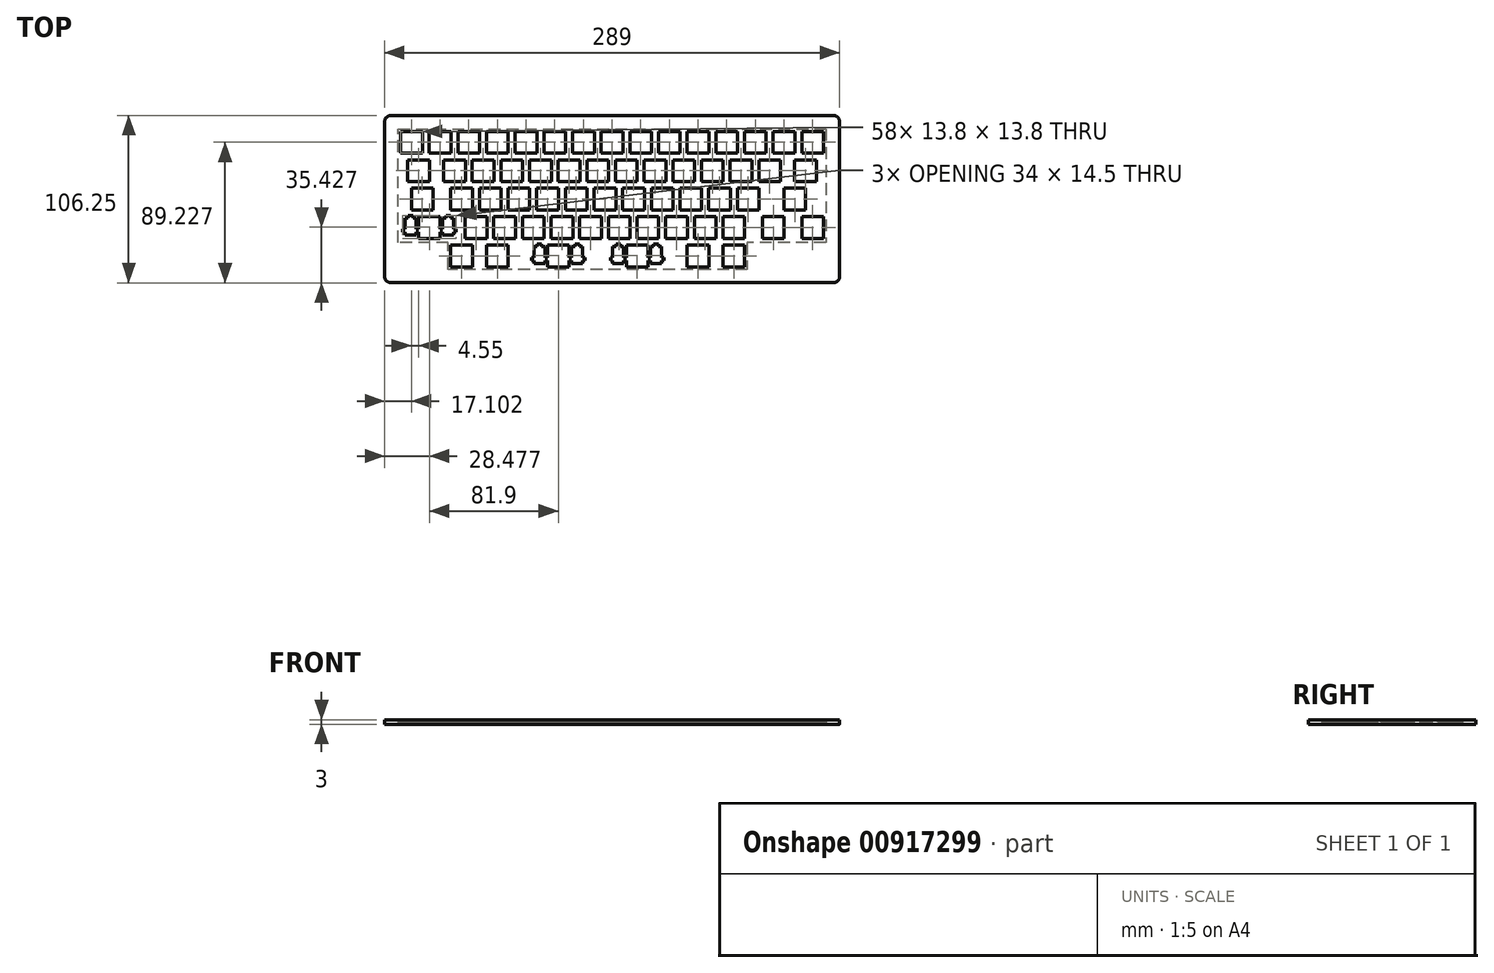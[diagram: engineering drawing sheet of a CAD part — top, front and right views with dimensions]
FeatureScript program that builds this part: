
annotation { "Feature Type Name" : "Feature", "Feature Type Description" : "" }
export const myFeature = defineFeature(function(context is Context, id is Id, definition is map)
    precondition{}
    {
        {
            var Q0;
            Q0=qCreatedBy(makeId("Top.planeOp"),FACE);
            var sketch = newSketch(context, id + "F0", { "sketchPlane" : qUnion([Q0])});
            skLineSegment(sketch, "E0.bottom", {"start": v(-54.29, -27.5) * mm, "end": v(-72.49, -27.5) * mm, "construction": true});
            skLineSegment(sketch, "E0.top", {"start": v(-54.29, -9.45) * mm, "end": v(-72.49, -9.45) * mm, "construction": true});
            skLineSegment(sketch, "E0.left", {"start": v(-54.29, -27.5) * mm, "end": v(-54.29, -9.45) * mm, "construction": true});
            skLineSegment(sketch, "E0.right", {"start": v(-72.49, -27.5) * mm, "end": v(-72.49, -9.45) * mm, "construction": true});
            skPoint(sketch, "E0.middle", {"position": v(-63.39, -18.47) * mm});
            skLineSegment(sketch, "E1.1.0.0", {"start": v(-36.09, -27.5) * mm, "end": v(-36.09, -9.45) * mm, "construction": true});
            skLineSegment(sketch, "E1.1.0.1", {"start": v(-36.09, -9.45) * mm, "end": v(-54.29, -9.45) * mm, "construction": true});
            skLineSegment(sketch, "E1.1.0.3", {"start": v(-36.09, -27.5) * mm, "end": v(-54.29, -27.5) * mm, "construction": true});
            skLineSegment(sketch, "E1.2.0.0", {"start": v(-17.89, -27.5) * mm, "end": v(-17.89, -9.45) * mm, "construction": true});
            skLineSegment(sketch, "E1.2.0.1", {"start": v(-17.89, -9.45) * mm, "end": v(-36.09, -9.45) * mm, "construction": true});
            skLineSegment(sketch, "E1.2.0.2", {"start": v(-36.09, -27.5) * mm, "end": v(-36.09, -9.45) * mm, "construction": true});
            skLineSegment(sketch, "E1.2.0.3", {"start": v(-17.89, -27.5) * mm, "end": v(-36.09, -27.5) * mm, "construction": true});
            skLineSegment(sketch, "E1.3.0.0", {"start": v(0.31, -27.5) * mm, "end": v(0.31, -9.45) * mm, "construction": true});
            skLineSegment(sketch, "E1.3.0.1", {"start": v(0.31, -9.45) * mm, "end": v(-17.89, -9.45) * mm, "construction": true});
            skLineSegment(sketch, "E1.3.0.2", {"start": v(-17.89, -27.5) * mm, "end": v(-17.89, -9.45) * mm, "construction": true});
            skLineSegment(sketch, "E1.3.0.3", {"start": v(0.31, -27.5) * mm, "end": v(-17.89, -27.5) * mm, "construction": true});
            skLineSegment(sketch, "E1.4.0.0", {"start": v(18.51, -27.5) * mm, "end": v(18.51, -9.45) * mm, "construction": true});
            skLineSegment(sketch, "E1.4.0.1", {"start": v(18.51, -9.45) * mm, "end": v(0.31, -9.45) * mm, "construction": true});
            skLineSegment(sketch, "E1.4.0.2", {"start": v(0.31, -27.5) * mm, "end": v(0.31, -9.45) * mm, "construction": true});
            skLineSegment(sketch, "E1.4.0.3", {"start": v(18.51, -27.5) * mm, "end": v(0.31, -27.5) * mm, "construction": true});
            skLineSegment(sketch, "E1.5.0.0", {"start": v(36.71, -27.5) * mm, "end": v(36.71, -9.45) * mm, "construction": true});
            skLineSegment(sketch, "E1.5.0.1", {"start": v(36.71, -9.45) * mm, "end": v(18.51, -9.45) * mm, "construction": true});
            skLineSegment(sketch, "E1.5.0.2", {"start": v(18.51, -27.5) * mm, "end": v(18.51, -9.45) * mm, "construction": true});
            skLineSegment(sketch, "E1.5.0.3", {"start": v(36.71, -27.5) * mm, "end": v(18.51, -27.5) * mm, "construction": true});
            skLineSegment(sketch, "E1.6.0.0", {"start": v(54.91, -27.5) * mm, "end": v(54.91, -9.45) * mm, "construction": true});
            skLineSegment(sketch, "E1.6.0.1", {"start": v(54.91, -9.45) * mm, "end": v(36.71, -9.45) * mm, "construction": true});
            skLineSegment(sketch, "E1.6.0.2", {"start": v(36.71, -27.5) * mm, "end": v(36.71, -9.45) * mm, "construction": true});
            skLineSegment(sketch, "E1.6.0.3", {"start": v(54.91, -27.5) * mm, "end": v(36.71, -27.5) * mm, "construction": true});
            skLineSegment(sketch, "E1.7.0.0", {"start": v(73.11, -27.5) * mm, "end": v(73.11, -9.45) * mm, "construction": true});
            skLineSegment(sketch, "E1.7.0.1", {"start": v(73.11, -9.45) * mm, "end": v(54.91, -9.45) * mm, "construction": true});
            skLineSegment(sketch, "E1.7.0.2", {"start": v(54.91, -27.5) * mm, "end": v(54.91, -9.45) * mm, "construction": true});
            skLineSegment(sketch, "E1.7.0.3", {"start": v(73.11, -27.5) * mm, "end": v(54.91, -27.5) * mm, "construction": true});
            skLineSegment(sketch, "E1.8.0.0", {"start": v(91.31, -27.5) * mm, "end": v(91.31, -9.45) * mm, "construction": true});
            skLineSegment(sketch, "E1.8.0.1", {"start": v(91.31, -9.45) * mm, "end": v(73.11, -9.45) * mm, "construction": true});
            skLineSegment(sketch, "E1.8.0.2", {"start": v(73.11, -27.5) * mm, "end": v(73.11, -9.45) * mm, "construction": true});
            skLineSegment(sketch, "E1.8.0.3", {"start": v(91.31, -27.5) * mm, "end": v(73.11, -27.5) * mm, "construction": true});
            skLineSegment(sketch, "E1.9.0.0", {"start": v(109.51, -27.5) * mm, "end": v(109.51, -9.45) * mm, "construction": true});
            skLineSegment(sketch, "E1.9.0.1", {"start": v(109.51, -9.45) * mm, "end": v(91.31, -9.45) * mm, "construction": true});
            skLineSegment(sketch, "E1.9.0.2", {"start": v(91.31, -27.5) * mm, "end": v(91.31, -9.45) * mm, "construction": true});
            skLineSegment(sketch, "E1.9.0.3", {"start": v(109.51, -27.5) * mm, "end": v(91.31, -27.5) * mm, "construction": true});
            skLineSegment(sketch, "E1.10.0.0", {"start": v(127.71, -27.5) * mm, "end": v(127.71, -9.45) * mm, "construction": true});
            skLineSegment(sketch, "E1.10.0.1", {"start": v(127.71, -9.45) * mm, "end": v(109.51, -9.45) * mm, "construction": true});
            skLineSegment(sketch, "E1.10.0.2", {"start": v(109.51, -27.5) * mm, "end": v(109.51, -9.45) * mm, "construction": true});
            skLineSegment(sketch, "E1.10.0.3", {"start": v(127.71, -27.5) * mm, "end": v(109.51, -27.5) * mm, "construction": true});
            skLineSegment(sketch, "E1.11.0.0", {"start": v(145.91, -27.5) * mm, "end": v(145.91, -9.45) * mm, "construction": true});
            skLineSegment(sketch, "E1.11.0.1", {"start": v(145.91, -9.45) * mm, "end": v(127.71, -9.45) * mm, "construction": true});
            skLineSegment(sketch, "E1.11.0.2", {"start": v(127.71, -27.5) * mm, "end": v(127.71, -9.45) * mm, "construction": true});
            skLineSegment(sketch, "E1.11.0.3", {"start": v(145.91, -27.5) * mm, "end": v(127.71, -27.5) * mm, "construction": true});
            skLineSegment(sketch, "E1.12.0.0", {"start": v(164.11, -27.5) * mm, "end": v(164.11, -9.45) * mm, "construction": true});
            skLineSegment(sketch, "E1.12.0.1", {"start": v(164.11, -9.45) * mm, "end": v(145.91, -9.45) * mm, "construction": true});
            skLineSegment(sketch, "E1.12.0.2", {"start": v(145.91, -27.5) * mm, "end": v(145.91, -9.45) * mm, "construction": true});
            skLineSegment(sketch, "E1.12.0.3", {"start": v(164.11, -27.5) * mm, "end": v(145.91, -27.5) * mm, "construction": true});
            skLineSegment(sketch, "E1.13.0.0", {"start": v(182.31, -27.5) * mm, "end": v(182.31, -9.45) * mm, "construction": true});
            skLineSegment(sketch, "E1.13.0.1", {"start": v(182.31, -9.45) * mm, "end": v(164.11, -9.45) * mm, "construction": true});
            skLineSegment(sketch, "E1.13.0.2", {"start": v(164.11, -27.5) * mm, "end": v(164.11, -9.45) * mm, "construction": true});
            skLineSegment(sketch, "E1.13.0.3", {"start": v(182.31, -27.5) * mm, "end": v(164.11, -27.5) * mm, "construction": true});
            skLineSegment(sketch, "E1.14.0.0", {"start": v(200.51, -27.5) * mm, "end": v(200.51, -9.45) * mm, "construction": true});
            skLineSegment(sketch, "E1.14.0.1", {"start": v(200.51, -9.45) * mm, "end": v(182.31, -9.45) * mm, "construction": true});
            skLineSegment(sketch, "E1.14.0.2", {"start": v(182.31, -27.5) * mm, "end": v(182.31, -9.45) * mm, "construction": true});
            skLineSegment(sketch, "E1.14.0.3", {"start": v(200.51, -27.5) * mm, "end": v(182.31, -27.5) * mm, "construction": true});
            skLineSegment(sketch, "E1.direction1", {"start": v(-72.49, -27.5) * mm, "end": v(-54.29, -27.5) * mm, "construction": true});
            skLineSegment(sketch, "E2.bottom", {"start": v(-72.49, -27.5) * mm, "end": v(-45.19, -27.5) * mm, "construction": true});
            skLineSegment(sketch, "E2.top", {"start": v(-72.49, -45.55) * mm, "end": v(-45.19, -45.55) * mm, "construction": true});
            skLineSegment(sketch, "E2.left", {"start": v(-72.49, -27.5) * mm, "end": v(-72.49, -45.55) * mm, "construction": true});
            skLineSegment(sketch, "E2.right", {"start": v(-45.19, -27.5) * mm, "end": v(-45.19, -45.55) * mm, "construction": true});
            skLineSegment(sketch, "E3.bottom", {"start": v(-45.19, -45.55) * mm, "end": v(-26.99, -45.55) * mm, "construction": true});
            skLineSegment(sketch, "E3.top", {"start": v(-45.19, -27.5) * mm, "end": v(-26.99, -27.5) * mm, "construction": true});
            skLineSegment(sketch, "E3.left", {"start": v(-45.19, -45.55) * mm, "end": v(-45.19, -27.5) * mm, "construction": true});
            skLineSegment(sketch, "E3.right", {"start": v(-26.99, -45.55) * mm, "end": v(-26.99, -27.5) * mm, "construction": true});
            skLineSegment(sketch, "E4.1.0.0", {"start": v(-26.99, -45.55) * mm, "end": v(-8.79, -45.55) * mm, "construction": true});
            skLineSegment(sketch, "E4.1.0.1", {"start": v(-26.99, -27.5) * mm, "end": v(-8.79, -27.5) * mm, "construction": true});
            skLineSegment(sketch, "E4.1.0.2", {"start": v(-26.99, -27.5) * mm, "end": v(-26.99, -45.55) * mm, "construction": true});
            skLineSegment(sketch, "E4.1.0.3", {"start": v(-8.79, -45.55) * mm, "end": v(-8.79, -27.5) * mm, "construction": true});
            skLineSegment(sketch, "E4.2.0.0", {"start": v(-8.79, -45.55) * mm, "end": v(9.41, -45.55) * mm, "construction": true});
            skLineSegment(sketch, "E4.2.0.1", {"start": v(-8.79, -27.5) * mm, "end": v(9.41, -27.5) * mm, "construction": true});
            skLineSegment(sketch, "E4.2.0.2", {"start": v(-8.79, -27.5) * mm, "end": v(-8.79, -45.55) * mm, "construction": true});
            skLineSegment(sketch, "E4.2.0.3", {"start": v(9.41, -45.55) * mm, "end": v(9.41, -27.5) * mm, "construction": true});
            skLineSegment(sketch, "E4.2.0.4", {"start": v(-8.79, -45.55) * mm, "end": v(-8.79, -27.5) * mm, "construction": true});
            skLineSegment(sketch, "E4.3.0.0", {"start": v(9.41, -45.55) * mm, "end": v(27.61, -45.55) * mm, "construction": true});
            skLineSegment(sketch, "E4.3.0.1", {"start": v(9.41, -27.5) * mm, "end": v(27.61, -27.5) * mm, "construction": true});
            skLineSegment(sketch, "E4.3.0.2", {"start": v(9.41, -27.5) * mm, "end": v(9.41, -45.55) * mm, "construction": true});
            skLineSegment(sketch, "E4.3.0.3", {"start": v(27.61, -45.55) * mm, "end": v(27.61, -27.5) * mm, "construction": true});
            skLineSegment(sketch, "E4.3.0.4", {"start": v(9.41, -45.55) * mm, "end": v(9.41, -27.5) * mm, "construction": true});
            skLineSegment(sketch, "E4.4.0.0", {"start": v(27.61, -45.55) * mm, "end": v(45.81, -45.55) * mm, "construction": true});
            skLineSegment(sketch, "E4.4.0.1", {"start": v(27.61, -27.5) * mm, "end": v(45.81, -27.5) * mm, "construction": true});
            skLineSegment(sketch, "E4.4.0.2", {"start": v(27.61, -27.5) * mm, "end": v(27.61, -45.55) * mm, "construction": true});
            skLineSegment(sketch, "E4.4.0.3", {"start": v(45.81, -45.55) * mm, "end": v(45.81, -27.5) * mm, "construction": true});
            skLineSegment(sketch, "E4.4.0.4", {"start": v(27.61, -45.55) * mm, "end": v(27.61, -27.5) * mm, "construction": true});
            skLineSegment(sketch, "E4.5.0.0", {"start": v(45.81, -45.55) * mm, "end": v(64.01, -45.55) * mm, "construction": true});
            skLineSegment(sketch, "E4.5.0.1", {"start": v(45.81, -27.5) * mm, "end": v(64.01, -27.5) * mm, "construction": true});
            skLineSegment(sketch, "E4.5.0.2", {"start": v(45.81, -27.5) * mm, "end": v(45.81, -45.55) * mm, "construction": true});
            skLineSegment(sketch, "E4.5.0.3", {"start": v(64.01, -45.55) * mm, "end": v(64.01, -27.5) * mm, "construction": true});
            skLineSegment(sketch, "E4.5.0.4", {"start": v(45.81, -45.55) * mm, "end": v(45.81, -27.5) * mm, "construction": true});
            skLineSegment(sketch, "E4.6.0.0", {"start": v(64.01, -45.55) * mm, "end": v(82.21, -45.55) * mm, "construction": true});
            skLineSegment(sketch, "E4.6.0.1", {"start": v(64.01, -27.5) * mm, "end": v(82.21, -27.5) * mm, "construction": true});
            skLineSegment(sketch, "E4.6.0.2", {"start": v(64.01, -27.5) * mm, "end": v(64.01, -45.55) * mm, "construction": true});
            skLineSegment(sketch, "E4.6.0.3", {"start": v(82.21, -45.55) * mm, "end": v(82.21, -27.5) * mm, "construction": true});
            skLineSegment(sketch, "E4.6.0.4", {"start": v(64.01, -45.55) * mm, "end": v(64.01, -27.5) * mm, "construction": true});
            skLineSegment(sketch, "E4.7.0.0", {"start": v(82.21, -45.55) * mm, "end": v(100.41, -45.55) * mm, "construction": true});
            skLineSegment(sketch, "E4.7.0.1", {"start": v(82.21, -27.5) * mm, "end": v(100.41, -27.5) * mm, "construction": true});
            skLineSegment(sketch, "E4.7.0.2", {"start": v(82.21, -27.5) * mm, "end": v(82.21, -45.55) * mm, "construction": true});
            skLineSegment(sketch, "E4.7.0.3", {"start": v(100.41, -45.55) * mm, "end": v(100.41, -27.5) * mm, "construction": true});
            skLineSegment(sketch, "E4.7.0.4", {"start": v(82.21, -45.55) * mm, "end": v(82.21, -27.5) * mm, "construction": true});
            skLineSegment(sketch, "E4.8.0.0", {"start": v(100.41, -45.55) * mm, "end": v(118.61, -45.55) * mm, "construction": true});
            skLineSegment(sketch, "E4.8.0.1", {"start": v(100.41, -27.5) * mm, "end": v(118.61, -27.5) * mm, "construction": true});
            skLineSegment(sketch, "E4.8.0.2", {"start": v(100.41, -27.5) * mm, "end": v(100.41, -45.55) * mm, "construction": true});
            skLineSegment(sketch, "E4.8.0.3", {"start": v(118.61, -45.55) * mm, "end": v(118.61, -27.5) * mm, "construction": true});
            skLineSegment(sketch, "E4.8.0.4", {"start": v(100.41, -45.55) * mm, "end": v(100.41, -27.5) * mm, "construction": true});
            skLineSegment(sketch, "E4.9.0.0", {"start": v(118.61, -45.55) * mm, "end": v(136.81, -45.55) * mm, "construction": true});
            skLineSegment(sketch, "E4.9.0.1", {"start": v(118.61, -27.5) * mm, "end": v(136.81, -27.5) * mm, "construction": true});
            skLineSegment(sketch, "E4.9.0.2", {"start": v(118.61, -27.5) * mm, "end": v(118.61, -45.55) * mm, "construction": true});
            skLineSegment(sketch, "E4.9.0.3", {"start": v(136.81, -45.55) * mm, "end": v(136.81, -27.5) * mm, "construction": true});
            skLineSegment(sketch, "E4.9.0.4", {"start": v(118.61, -45.55) * mm, "end": v(118.61, -27.5) * mm, "construction": true});
            skLineSegment(sketch, "E4.10.0.0", {"start": v(136.81, -45.55) * mm, "end": v(155.01, -45.55) * mm, "construction": true});
            skLineSegment(sketch, "E4.10.0.1", {"start": v(136.81, -27.5) * mm, "end": v(155.01, -27.5) * mm, "construction": true});
            skLineSegment(sketch, "E4.10.0.2", {"start": v(136.81, -27.5) * mm, "end": v(136.81, -45.55) * mm, "construction": true});
            skLineSegment(sketch, "E4.10.0.3", {"start": v(155.01, -45.55) * mm, "end": v(155.01, -27.5) * mm, "construction": true});
            skLineSegment(sketch, "E4.10.0.4", {"start": v(136.81, -45.55) * mm, "end": v(136.81, -27.5) * mm, "construction": true});
            skLineSegment(sketch, "E4.11.0.0", {"start": v(155.01, -45.55) * mm, "end": v(173.21, -45.55) * mm, "construction": true});
            skLineSegment(sketch, "E4.11.0.1", {"start": v(155.01, -27.5) * mm, "end": v(173.21, -27.5) * mm, "construction": true});
            skLineSegment(sketch, "E4.11.0.2", {"start": v(155.01, -27.5) * mm, "end": v(155.01, -45.55) * mm, "construction": true});
            skLineSegment(sketch, "E4.11.0.3", {"start": v(173.21, -45.55) * mm, "end": v(173.21, -27.5) * mm, "construction": true});
            skLineSegment(sketch, "E4.11.0.4", {"start": v(155.01, -45.55) * mm, "end": v(155.01, -27.5) * mm, "construction": true});
            skLineSegment(sketch, "E5.bottom", {"start": v(173.21, -45.55) * mm, "end": v(200.51, -45.55) * mm, "construction": true});
            skLineSegment(sketch, "E5.top", {"start": v(173.21, -27.5) * mm, "end": v(200.51, -27.5) * mm, "construction": true});
            skLineSegment(sketch, "E5.right", {"start": v(200.51, -45.55) * mm, "end": v(200.51, -27.5) * mm, "construction": true});
            skLineSegment(sketch, "E6.bottom", {"start": v(-72.49, -45.55) * mm, "end": v(-40.64, -45.55) * mm, "construction": true});
            skLineSegment(sketch, "E6.top", {"start": v(-72.49, -63.6) * mm, "end": v(-40.64, -63.6) * mm, "construction": true});
            skLineSegment(sketch, "E6.left", {"start": v(-72.49, -45.55) * mm, "end": v(-72.49, -63.6) * mm, "construction": true});
            skLineSegment(sketch, "E6.right", {"start": v(-40.64, -45.55) * mm, "end": v(-40.64, -63.6) * mm, "construction": true});
            skLineSegment(sketch, "E7.bottom", {"start": v(-40.64, -63.6) * mm, "end": v(-22.44, -63.6) * mm, "construction": true});
            skLineSegment(sketch, "E7.top", {"start": v(-40.64, -45.55) * mm, "end": v(-22.44, -45.55) * mm, "construction": true});
            skLineSegment(sketch, "E7.left", {"start": v(-40.64, -63.6) * mm, "end": v(-40.64, -45.55) * mm, "construction": true});
            skLineSegment(sketch, "E7.right", {"start": v(-22.44, -63.6) * mm, "end": v(-22.44, -45.55) * mm, "construction": true});
            skLineSegment(sketch, "E8.1.0.0", {"start": v(-22.44, -63.6) * mm, "end": v(-4.24, -63.6) * mm, "construction": true});
            skLineSegment(sketch, "E8.1.0.1", {"start": v(-22.44, -45.55) * mm, "end": v(-4.24, -45.55) * mm, "construction": true});
            skLineSegment(sketch, "E8.1.0.2", {"start": v(-4.24, -63.6) * mm, "end": v(-4.24, -45.55) * mm, "construction": true});
            skLineSegment(sketch, "E8.1.0.3", {"start": v(-22.44, -45.55) * mm, "end": v(-22.44, -63.6) * mm, "construction": true});
            skLineSegment(sketch, "E8.2.0.0", {"start": v(-4.24, -63.6) * mm, "end": v(13.96, -63.6) * mm, "construction": true});
            skLineSegment(sketch, "E8.2.0.1", {"start": v(-4.24, -45.55) * mm, "end": v(13.96, -45.55) * mm, "construction": true});
            skLineSegment(sketch, "E8.2.0.2", {"start": v(13.96, -63.6) * mm, "end": v(13.96, -45.55) * mm, "construction": true});
            skLineSegment(sketch, "E8.2.0.3", {"start": v(-4.24, -45.55) * mm, "end": v(-4.24, -63.6) * mm, "construction": true});
            skLineSegment(sketch, "E8.2.0.4", {"start": v(-4.24, -63.6) * mm, "end": v(-4.24, -45.55) * mm, "construction": true});
            skLineSegment(sketch, "E8.3.0.0", {"start": v(13.96, -63.6) * mm, "end": v(32.16, -63.6) * mm, "construction": true});
            skLineSegment(sketch, "E8.3.0.1", {"start": v(13.96, -45.55) * mm, "end": v(32.16, -45.55) * mm, "construction": true});
            skLineSegment(sketch, "E8.3.0.2", {"start": v(32.16, -63.6) * mm, "end": v(32.16, -45.55) * mm, "construction": true});
            skLineSegment(sketch, "E8.3.0.3", {"start": v(13.96, -45.55) * mm, "end": v(13.96, -63.6) * mm, "construction": true});
            skLineSegment(sketch, "E8.3.0.4", {"start": v(13.96, -63.6) * mm, "end": v(13.96, -45.55) * mm, "construction": true});
            skLineSegment(sketch, "E8.4.0.0", {"start": v(32.16, -63.6) * mm, "end": v(50.36, -63.6) * mm, "construction": true});
            skLineSegment(sketch, "E8.4.0.1", {"start": v(32.16, -45.55) * mm, "end": v(50.36, -45.55) * mm, "construction": true});
            skLineSegment(sketch, "E8.4.0.2", {"start": v(50.36, -63.6) * mm, "end": v(50.36, -45.55) * mm, "construction": true});
            skLineSegment(sketch, "E8.4.0.3", {"start": v(32.16, -45.55) * mm, "end": v(32.16, -63.6) * mm, "construction": true});
            skLineSegment(sketch, "E8.4.0.4", {"start": v(32.16, -63.6) * mm, "end": v(32.16, -45.55) * mm, "construction": true});
            skLineSegment(sketch, "E8.5.0.0", {"start": v(50.36, -63.6) * mm, "end": v(68.56, -63.6) * mm, "construction": true});
            skLineSegment(sketch, "E8.5.0.1", {"start": v(50.36, -45.55) * mm, "end": v(68.56, -45.55) * mm, "construction": true});
            skLineSegment(sketch, "E8.5.0.2", {"start": v(68.56, -63.6) * mm, "end": v(68.56, -45.55) * mm, "construction": true});
            skLineSegment(sketch, "E8.5.0.3", {"start": v(50.36, -45.55) * mm, "end": v(50.36, -63.6) * mm, "construction": true});
            skLineSegment(sketch, "E8.5.0.4", {"start": v(50.36, -63.6) * mm, "end": v(50.36, -45.55) * mm, "construction": true});
            skLineSegment(sketch, "E8.6.0.0", {"start": v(68.56, -63.6) * mm, "end": v(86.76, -63.6) * mm, "construction": true});
            skLineSegment(sketch, "E8.6.0.1", {"start": v(68.56, -45.55) * mm, "end": v(86.76, -45.55) * mm, "construction": true});
            skLineSegment(sketch, "E8.6.0.2", {"start": v(86.76, -63.6) * mm, "end": v(86.76, -45.55) * mm, "construction": true});
            skLineSegment(sketch, "E8.6.0.3", {"start": v(68.56, -45.55) * mm, "end": v(68.56, -63.6) * mm, "construction": true});
            skLineSegment(sketch, "E8.6.0.4", {"start": v(68.56, -63.6) * mm, "end": v(68.56, -45.55) * mm, "construction": true});
            skLineSegment(sketch, "E8.7.0.0", {"start": v(86.76, -63.6) * mm, "end": v(104.96, -63.6) * mm, "construction": true});
            skLineSegment(sketch, "E8.7.0.1", {"start": v(86.76, -45.55) * mm, "end": v(104.96, -45.55) * mm, "construction": true});
            skLineSegment(sketch, "E8.7.0.2", {"start": v(104.96, -63.6) * mm, "end": v(104.96, -45.55) * mm, "construction": true});
            skLineSegment(sketch, "E8.7.0.3", {"start": v(86.76, -45.55) * mm, "end": v(86.76, -63.6) * mm, "construction": true});
            skLineSegment(sketch, "E8.7.0.4", {"start": v(86.76, -63.6) * mm, "end": v(86.76, -45.55) * mm, "construction": true});
            skLineSegment(sketch, "E8.8.0.0", {"start": v(104.96, -63.6) * mm, "end": v(123.16, -63.6) * mm, "construction": true});
            skLineSegment(sketch, "E8.8.0.1", {"start": v(104.96, -45.55) * mm, "end": v(123.16, -45.55) * mm, "construction": true});
            skLineSegment(sketch, "E8.8.0.2", {"start": v(123.16, -63.6) * mm, "end": v(123.16, -45.55) * mm, "construction": true});
            skLineSegment(sketch, "E8.8.0.3", {"start": v(104.96, -45.55) * mm, "end": v(104.96, -63.6) * mm, "construction": true});
            skLineSegment(sketch, "E8.8.0.4", {"start": v(104.96, -63.6) * mm, "end": v(104.96, -45.55) * mm, "construction": true});
            skLineSegment(sketch, "E8.9.0.0", {"start": v(123.16, -63.6) * mm, "end": v(141.36, -63.6) * mm, "construction": true});
            skLineSegment(sketch, "E8.9.0.1", {"start": v(123.16, -45.55) * mm, "end": v(141.36, -45.55) * mm, "construction": true});
            skLineSegment(sketch, "E8.9.0.2", {"start": v(141.36, -63.6) * mm, "end": v(141.36, -45.55) * mm, "construction": true});
            skLineSegment(sketch, "E8.9.0.3", {"start": v(123.16, -45.55) * mm, "end": v(123.16, -63.6) * mm, "construction": true});
            skLineSegment(sketch, "E8.9.0.4", {"start": v(123.16, -63.6) * mm, "end": v(123.16, -45.55) * mm, "construction": true});
            skLineSegment(sketch, "E8.10.0.0", {"start": v(141.36, -63.6) * mm, "end": v(159.56, -63.6) * mm, "construction": true});
            skLineSegment(sketch, "E8.10.0.1", {"start": v(141.36, -45.55) * mm, "end": v(159.56, -45.55) * mm, "construction": true});
            skLineSegment(sketch, "E8.10.0.2", {"start": v(159.56, -63.6) * mm, "end": v(159.56, -45.55) * mm, "construction": true});
            skLineSegment(sketch, "E8.10.0.3", {"start": v(141.36, -45.55) * mm, "end": v(141.36, -63.6) * mm, "construction": true});
            skLineSegment(sketch, "E8.10.0.4", {"start": v(141.36, -63.6) * mm, "end": v(141.36, -45.55) * mm, "construction": true});
            skLineSegment(sketch, "E9.bottom", {"start": v(159.56, -63.6) * mm, "end": v(200.51, -63.6) * mm, "construction": true});
            skLineSegment(sketch, "E9.top", {"start": v(159.56, -45.55) * mm, "end": v(200.51, -45.55) * mm, "construction": true});
            skLineSegment(sketch, "E9.right", {"start": v(200.51, -63.6) * mm, "end": v(200.51, -45.55) * mm, "construction": true});
            skLineSegment(sketch, "E10.bottom", {"start": v(-72.49, -63.6) * mm, "end": v(-31.54, -63.6) * mm, "construction": true});
            skLineSegment(sketch, "E10.top", {"start": v(-72.49, -81.65) * mm, "end": v(-31.54, -81.65) * mm, "construction": true});
            skLineSegment(sketch, "E10.left", {"start": v(-72.49, -63.6) * mm, "end": v(-72.49, -81.65) * mm, "construction": true});
            skLineSegment(sketch, "E10.right", {"start": v(-31.54, -63.6) * mm, "end": v(-31.54, -81.65) * mm, "construction": true});
            skLineSegment(sketch, "E11.bottom", {"start": v(-31.54, -81.65) * mm, "end": v(-13.34, -81.65) * mm, "construction": true});
            skLineSegment(sketch, "E11.top", {"start": v(-31.54, -63.6) * mm, "end": v(-13.34, -63.6) * mm, "construction": true});
            skLineSegment(sketch, "E11.left", {"start": v(-31.54, -81.65) * mm, "end": v(-31.54, -63.6) * mm, "construction": true});
            skLineSegment(sketch, "E11.right", {"start": v(-13.34, -81.65) * mm, "end": v(-13.34, -63.6) * mm, "construction": true});
            skLineSegment(sketch, "E12.1.0.0", {"start": v(-13.34, -81.65) * mm, "end": v(4.86, -81.65) * mm, "construction": true});
            skLineSegment(sketch, "E12.1.0.1", {"start": v(4.86, -81.65) * mm, "end": v(4.86, -63.6) * mm, "construction": true});
            skLineSegment(sketch, "E12.1.0.2", {"start": v(-13.34, -63.6) * mm, "end": v(-13.34, -81.65) * mm, "construction": true});
            skLineSegment(sketch, "E12.1.0.3", {"start": v(-13.34, -63.6) * mm, "end": v(4.86, -63.6) * mm, "construction": true});
            skLineSegment(sketch, "E12.2.0.0", {"start": v(4.86, -81.65) * mm, "end": v(23.06, -81.65) * mm, "construction": true});
            skLineSegment(sketch, "E12.2.0.1", {"start": v(23.06, -81.65) * mm, "end": v(23.06, -63.6) * mm, "construction": true});
            skLineSegment(sketch, "E12.2.0.2", {"start": v(4.86, -63.6) * mm, "end": v(4.86, -81.65) * mm, "construction": true});
            skLineSegment(sketch, "E12.2.0.3", {"start": v(4.86, -63.6) * mm, "end": v(23.06, -63.6) * mm, "construction": true});
            skLineSegment(sketch, "E12.2.0.4", {"start": v(4.86, -81.65) * mm, "end": v(4.86, -63.6) * mm, "construction": true});
            skLineSegment(sketch, "E12.3.0.0", {"start": v(23.06, -81.65) * mm, "end": v(41.26, -81.65) * mm, "construction": true});
            skLineSegment(sketch, "E12.3.0.1", {"start": v(41.26, -81.65) * mm, "end": v(41.26, -63.6) * mm, "construction": true});
            skLineSegment(sketch, "E12.3.0.2", {"start": v(23.06, -63.6) * mm, "end": v(23.06, -81.65) * mm, "construction": true});
            skLineSegment(sketch, "E12.3.0.3", {"start": v(23.06, -63.6) * mm, "end": v(41.26, -63.6) * mm, "construction": true});
            skLineSegment(sketch, "E12.3.0.4", {"start": v(23.06, -81.65) * mm, "end": v(23.06, -63.6) * mm, "construction": true});
            skLineSegment(sketch, "E12.4.0.0", {"start": v(41.26, -81.65) * mm, "end": v(59.46, -81.65) * mm, "construction": true});
            skLineSegment(sketch, "E12.4.0.1", {"start": v(59.46, -81.65) * mm, "end": v(59.46, -63.6) * mm, "construction": true});
            skLineSegment(sketch, "E12.4.0.2", {"start": v(41.26, -63.6) * mm, "end": v(41.26, -81.65) * mm, "construction": true});
            skLineSegment(sketch, "E12.4.0.3", {"start": v(41.26, -63.6) * mm, "end": v(59.46, -63.6) * mm, "construction": true});
            skLineSegment(sketch, "E12.4.0.4", {"start": v(41.26, -81.65) * mm, "end": v(41.26, -63.6) * mm, "construction": true});
            skLineSegment(sketch, "E12.5.0.0", {"start": v(59.46, -81.65) * mm, "end": v(77.66, -81.65) * mm, "construction": true});
            skLineSegment(sketch, "E12.5.0.1", {"start": v(77.66, -81.65) * mm, "end": v(77.66, -63.6) * mm, "construction": true});
            skLineSegment(sketch, "E12.5.0.2", {"start": v(59.46, -63.6) * mm, "end": v(59.46, -81.65) * mm, "construction": true});
            skLineSegment(sketch, "E12.5.0.3", {"start": v(59.46, -63.6) * mm, "end": v(77.66, -63.6) * mm, "construction": true});
            skLineSegment(sketch, "E12.5.0.4", {"start": v(59.46, -81.65) * mm, "end": v(59.46, -63.6) * mm, "construction": true});
            skLineSegment(sketch, "E12.6.0.0", {"start": v(77.66, -81.65) * mm, "end": v(95.86, -81.65) * mm, "construction": true});
            skLineSegment(sketch, "E12.6.0.1", {"start": v(95.86, -81.65) * mm, "end": v(95.86, -63.6) * mm, "construction": true});
            skLineSegment(sketch, "E12.6.0.2", {"start": v(77.66, -63.6) * mm, "end": v(77.66, -81.65) * mm, "construction": true});
            skLineSegment(sketch, "E12.6.0.3", {"start": v(77.66, -63.6) * mm, "end": v(95.86, -63.6) * mm, "construction": true});
            skLineSegment(sketch, "E12.6.0.4", {"start": v(77.66, -81.65) * mm, "end": v(77.66, -63.6) * mm, "construction": true});
            skLineSegment(sketch, "E12.7.0.0", {"start": v(95.86, -81.65) * mm, "end": v(114.06, -81.65) * mm, "construction": true});
            skLineSegment(sketch, "E12.7.0.1", {"start": v(114.06, -81.65) * mm, "end": v(114.06, -63.6) * mm, "construction": true});
            skLineSegment(sketch, "E12.7.0.2", {"start": v(95.86, -63.6) * mm, "end": v(95.86, -81.65) * mm, "construction": true});
            skLineSegment(sketch, "E12.7.0.3", {"start": v(95.86, -63.6) * mm, "end": v(114.06, -63.6) * mm, "construction": true});
            skLineSegment(sketch, "E12.7.0.4", {"start": v(95.86, -81.65) * mm, "end": v(95.86, -63.6) * mm, "construction": true});
            skLineSegment(sketch, "E12.8.0.0", {"start": v(114.06, -81.65) * mm, "end": v(132.26, -81.65) * mm, "construction": true});
            skLineSegment(sketch, "E12.8.0.1", {"start": v(132.26, -81.65) * mm, "end": v(132.26, -63.6) * mm, "construction": true});
            skLineSegment(sketch, "E12.8.0.2", {"start": v(114.06, -63.6) * mm, "end": v(114.06, -81.65) * mm, "construction": true});
            skLineSegment(sketch, "E12.8.0.3", {"start": v(114.06, -63.6) * mm, "end": v(132.26, -63.6) * mm, "construction": true});
            skLineSegment(sketch, "E12.8.0.4", {"start": v(114.06, -81.65) * mm, "end": v(114.06, -63.6) * mm, "construction": true});
            skLineSegment(sketch, "E12.9.0.0", {"start": v(132.26, -81.65) * mm, "end": v(150.46, -81.65) * mm, "construction": true});
            skLineSegment(sketch, "E12.9.0.1", {"start": v(150.46, -81.65) * mm, "end": v(150.46, -63.6) * mm, "construction": true});
            skLineSegment(sketch, "E12.9.0.2", {"start": v(132.26, -63.6) * mm, "end": v(132.26, -81.65) * mm, "construction": true});
            skLineSegment(sketch, "E12.9.0.3", {"start": v(132.26, -63.6) * mm, "end": v(150.46, -63.6) * mm, "construction": true});
            skLineSegment(sketch, "E12.9.0.4", {"start": v(132.26, -81.65) * mm, "end": v(132.26, -63.6) * mm, "construction": true});
            skLineSegment(sketch, "E13.bottom", {"start": v(150.46, -81.65) * mm, "end": v(182.31, -81.65) * mm, "construction": true});
            skLineSegment(sketch, "E13.top", {"start": v(150.46, -63.6) * mm, "end": v(182.31, -63.6) * mm, "construction": true});
            skLineSegment(sketch, "E13.right", {"start": v(182.31, -81.65) * mm, "end": v(182.31, -63.6) * mm, "construction": true});
            skLineSegment(sketch, "E14.bottom", {"start": v(182.31, -81.65) * mm, "end": v(200.51, -81.65) * mm, "construction": true});
            skLineSegment(sketch, "E14.top", {"start": v(182.31, -63.6) * mm, "end": v(200.51, -63.6) * mm, "construction": true});
            skLineSegment(sketch, "E14.right", {"start": v(200.51, -81.65) * mm, "end": v(200.51, -63.6) * mm, "construction": true});
            skLineSegment(sketch, "E15.bottom", {"start": v(-72.49, -81.65) * mm, "end": v(-40.64, -81.65) * mm, "construction": true});
            skLineSegment(sketch, "E15.top", {"start": v(-72.49, -99.7) * mm, "end": v(-40.64, -99.7) * mm, "construction": true});
            skLineSegment(sketch, "E15.left", {"start": v(-72.49, -81.65) * mm, "end": v(-72.49, -99.7) * mm, "construction": true});
            skLineSegment(sketch, "E15.right", {"start": v(-40.64, -81.65) * mm, "end": v(-40.64, -99.7) * mm, "construction": true});
            skLineSegment(sketch, "E16.bottom", {"start": v(-40.64, -99.7) * mm, "end": v(-22.44, -99.7) * mm, "construction": true});
            skLineSegment(sketch, "E16.top", {"start": v(-40.64, -81.65) * mm, "end": v(-22.44, -81.65) * mm, "construction": true});
            skLineSegment(sketch, "E16.left", {"start": v(-40.64, -99.7) * mm, "end": v(-40.64, -81.65) * mm, "construction": true});
            skLineSegment(sketch, "E16.right", {"start": v(-22.44, -99.7) * mm, "end": v(-22.44, -81.65) * mm, "construction": true});
            skLineSegment(sketch, "E17.bottom", {"start": v(-22.44, -99.7) * mm, "end": v(4.86, -99.7) * mm, "construction": true});
            skLineSegment(sketch, "E17.top", {"start": v(-22.44, -81.65) * mm, "end": v(4.86, -81.65) * mm, "construction": true});
            skLineSegment(sketch, "E17.right", {"start": v(4.86, -99.7) * mm, "end": v(4.86, -81.65) * mm, "construction": true});
            skLineSegment(sketch, "E18.bottom", {"start": v(4.86, -99.7) * mm, "end": v(54.91, -99.7) * mm, "construction": true});
            skLineSegment(sketch, "E18.top", {"start": v(4.86, -81.65) * mm, "end": v(54.91, -81.65) * mm, "construction": true});
            skLineSegment(sketch, "E18.right", {"start": v(54.91, -99.7) * mm, "end": v(54.91, -81.65) * mm, "construction": true});
            skLineSegment(sketch, "E19.bottom", {"start": v(54.91, -99.7) * mm, "end": v(104.96, -99.7) * mm, "construction": true});
            skLineSegment(sketch, "E19.top", {"start": v(54.91, -81.65) * mm, "end": v(104.96, -81.65) * mm, "construction": true});
            skLineSegment(sketch, "E19.right", {"start": v(104.96, -99.7) * mm, "end": v(104.96, -81.65) * mm, "construction": true});
            skLineSegment(sketch, "E20.bottom", {"start": v(104.96, -99.7) * mm, "end": v(132.26, -99.7) * mm, "construction": true});
            skLineSegment(sketch, "E20.top", {"start": v(104.96, -81.65) * mm, "end": v(132.26, -81.65) * mm, "construction": true});
            skLineSegment(sketch, "E20.right", {"start": v(132.26, -99.7) * mm, "end": v(132.26, -81.65) * mm, "construction": true});
            skLineSegment(sketch, "E21.bottom", {"start": v(132.26, -99.7) * mm, "end": v(150.46, -99.7) * mm, "construction": true});
            skLineSegment(sketch, "E21.right", {"start": v(150.46, -99.7) * mm, "end": v(150.46, -81.65) * mm, "construction": true});
            skLineSegment(sketch, "E22.bottom", {"start": v(150.46, -99.7) * mm, "end": v(200.51, -99.7) * mm, "construction": true});
            skLineSegment(sketch, "E22.top", {"start": v(150.46, -81.65) * mm, "end": v(200.51, -81.65) * mm, "construction": true});
            skLineSegment(sketch, "E22.right", {"start": v(200.51, -99.7) * mm, "end": v(200.51, -81.65) * mm, "construction": true});
            skLineSegment(sketch, "E23.bottom", {"start": v(-56.49, -11.57) * mm, "end": v(-70.29, -11.57) * mm});
            skLineSegment(sketch, "E23.top", {"start": v(-56.49, -25.37) * mm, "end": v(-70.29, -25.37) * mm});
            skLineSegment(sketch, "E23.left", {"start": v(-56.49, -11.57) * mm, "end": v(-56.49, -25.37) * mm});
            skLineSegment(sketch, "E23.right", {"start": v(-70.29, -11.57) * mm, "end": v(-70.29, -25.37) * mm});
            skLineSegment(sketch, "E24.bottom", {"start": v(-51.94, -29.62) * mm, "end": v(-65.74, -29.62) * mm});
            skLineSegment(sketch, "E24.top", {"start": v(-51.94, -43.42) * mm, "end": v(-65.74, -43.42) * mm});
            skLineSegment(sketch, "E24.left", {"start": v(-51.94, -29.62) * mm, "end": v(-51.94, -43.42) * mm});
            skLineSegment(sketch, "E24.right", {"start": v(-65.74, -29.62) * mm, "end": v(-65.74, -43.42) * mm});
            skPoint(sketch, "E24.middle", {"position": v(-58.84, -36.52) * mm});
            skPoint(sketch, "E24.middle.positionSnap0", {"position": v(-72.49, -36.52) * mm});
            skPoint(sketch, "E24.middle.positionSnap1", {"position": v(-58.84, -45.55) * mm});
            skPoint(sketch, "E24.centerSnap0", {"position": v(-72.49, -36.52) * mm});
            skPoint(sketch, "E24.centerSnap1", {"position": v(-58.84, -45.55) * mm});
            skLineSegment(sketch, "E25.bottom", {"start": v(-49.66, -47.67) * mm, "end": v(-63.46, -47.67) * mm});
            skLineSegment(sketch, "E25.top", {"start": v(-49.66, -61.47) * mm, "end": v(-63.46, -61.47) * mm});
            skLineSegment(sketch, "E25.left", {"start": v(-49.66, -47.67) * mm, "end": v(-49.66, -61.47) * mm});
            skLineSegment(sketch, "E25.right", {"start": v(-63.46, -47.67) * mm, "end": v(-63.46, -61.47) * mm});
            skPoint(sketch, "E25.middle", {"position": v(-56.56, -54.57) * mm});
            skPoint(sketch, "E25.middle.positionSnap0", {"position": v(-72.49, -54.57) * mm});
            skPoint(sketch, "E25.middle.positionSnap1", {"position": v(-56.56, -63.6) * mm});
            skPoint(sketch, "E25.centerSnap0", {"position": v(-72.49, -54.57) * mm});
            skPoint(sketch, "E25.centerSnap1", {"position": v(-56.56, -63.6) * mm});
            skPoint(sketch, "E26.middle.positionSnap0", {"position": v(-56.56, -81.65) * mm});
            skPoint(sketch, "E26.middle.positionSnap1", {"position": v(-72.49, -72.62) * mm});
            skPoint(sketch, "E26.centerSnap0", {"position": v(-56.56, -81.65) * mm});
            skPoint(sketch, "E26.centerSnap1", {"position": v(-72.49, -72.62) * mm});
            skLineSegment(sketch, "E27.bottom", {"start": v(-24.64, -83.77) * mm, "end": v(-38.44, -83.77) * mm});
            skLineSegment(sketch, "E27.top", {"start": v(-24.64, -97.57) * mm, "end": v(-38.44, -97.57) * mm});
            skLineSegment(sketch, "E27.left", {"start": v(-24.64, -83.77) * mm, "end": v(-24.64, -97.57) * mm});
            skLineSegment(sketch, "E27.right", {"start": v(-38.44, -83.77) * mm, "end": v(-38.44, -97.57) * mm});
            skPoint(sketch, "E27.middle", {"position": v(-31.54, -90.67) * mm});
            skPoint(sketch, "E27.middle.positionSnap0", {"position": v(-40.64, -90.67) * mm});
            skPoint(sketch, "E27.middle.positionSnap1", {"position": v(-31.54, -99.7) * mm});
            skPoint(sketch, "E27.centerSnap0", {"position": v(-40.64, -90.67) * mm});
            skPoint(sketch, "E27.centerSnap1", {"position": v(-31.54, -99.7) * mm});
            skLineSegment(sketch, "E28.bottom", {"start": v(-45.11, -65.72) * mm, "end": v(-58.91, -65.72) * mm});
            skLineSegment(sketch, "E28.top", {"start": v(-45.11, -79.52) * mm, "end": v(-58.91, -79.52) * mm});
            skLineSegment(sketch, "E28.left", {"start": v(-45.11, -65.72) * mm, "end": v(-45.11, -79.52) * mm});
            skLineSegment(sketch, "E28.right", {"start": v(-58.91, -65.72) * mm, "end": v(-58.91, -79.52) * mm});
            skPoint(sketch, "E28.middle", {"position": v(-52.01, -72.62) * mm});
            skPoint(sketch, "E28.middle.positionSnap0", {"position": v(-52.01, -81.65) * mm});
            skPoint(sketch, "E28.centerSnap0", {"position": v(-52.01, -81.65) * mm});
            skLineSegment(sketch, "E29", {"start": v(-52.01, -79.52) * mm, "end": v(-52.01, -77.52) * mm, "construction": true});
            skLineSegment(sketch, "E30", {"start": v(-52.01, -77.52) * mm, "end": v(-67.51, -77.52) * mm, "construction": true});
            skLineSegment(sketch, "E31", {"start": v(-52.01, -77.52) * mm, "end": v(-36.51, -77.52) * mm, "construction": true});
            skLineSegment(sketch, "E32", {"start": v(-67.51, -77.52) * mm, "end": v(-60.51, -77.52) * mm});
            skLineSegment(sketch, "E33", {"start": v(-60.51, -77.52) * mm, "end": v(-60.51, -75.52) * mm});
            skLineSegment(sketch, "E34", {"start": v(-60.51, -75.52) * mm, "end": v(-58.91, -75.52) * mm});
            skLineSegment(sketch, "E35", {"start": v(-58.91, -75.52) * mm, "end": v(-58.91, -73.52) * mm});
            skLineSegment(sketch, "E36", {"start": v(-58.91, -73.52) * mm, "end": v(-60.51, -73.52) * mm});
            skLineSegment(sketch, "E37", {"start": v(-60.51, -73.52) * mm, "end": v(-60.51, -66.52) * mm});
            skLineSegment(sketch, "E38", {"start": v(-67.51, -77.52) * mm, "end": v(-67.51, -75.52) * mm});
            skLineSegment(sketch, "E39", {"start": v(-67.51, -75.52) * mm, "end": v(-69.01, -75.52) * mm});
            skLineSegment(sketch, "E40", {"start": v(-69.01, -75.52) * mm, "end": v(-69.01, -73.52) * mm});
            skLineSegment(sketch, "E41", {"start": v(-69.01, -73.52) * mm, "end": v(-67.51, -73.52) * mm});
            skLineSegment(sketch, "E42", {"start": v(-67.51, -73.52) * mm, "end": v(-67.51, -66.52) * mm});
            skLineSegment(sketch, "E43", {"start": v(-67.51, -66.52) * mm, "end": v(-65.51, -66.52) * mm});
            skLineSegment(sketch, "E44", {"start": v(-60.51, -66.52) * mm, "end": v(-62.51, -66.52) * mm});
            skLineSegment(sketch, "E45", {"start": v(-62.51, -66.52) * mm, "end": v(-62.51, -65.02) * mm});
            skLineSegment(sketch, "E46", {"start": v(-62.51, -65.02) * mm, "end": v(-65.51, -65.02) * mm});
            skLineSegment(sketch, "E47", {"start": v(-65.51, -65.02) * mm, "end": v(-65.51, -66.52) * mm});
            skLineSegment(sketch, "E48", {"start": v(-36.51, -77.52) * mm, "end": v(-36.51, -75.52) * mm});
            skLineSegment(sketch, "E49", {"start": v(-36.51, -75.52) * mm, "end": v(-35.01, -75.52) * mm});
            skLineSegment(sketch, "E50", {"start": v(-35.01, -75.52) * mm, "end": v(-35.01, -73.52) * mm});
            skLineSegment(sketch, "E51", {"start": v(-35.01, -73.52) * mm, "end": v(-36.51, -73.52) * mm});
            skLineSegment(sketch, "E52", {"start": v(-36.51, -73.52) * mm, "end": v(-36.51, -66.52) * mm});
            skLineSegment(sketch, "E53", {"start": v(-43.51, -77.52) * mm, "end": v(-43.51, -75.52) * mm});
            skLineSegment(sketch, "E54", {"start": v(-43.51, -75.52) * mm, "end": v(-45.11, -75.52) * mm});
            skLineSegment(sketch, "E55", {"start": v(-45.11, -75.52) * mm, "end": v(-45.11, -73.52) * mm});
            skLineSegment(sketch, "E56", {"start": v(-45.11, -73.52) * mm, "end": v(-43.51, -73.52) * mm});
            skLineSegment(sketch, "E57", {"start": v(-43.51, -73.52) * mm, "end": v(-43.51, -66.52) * mm});
            skLineSegment(sketch, "E58", {"start": v(-43.51, -66.52) * mm, "end": v(-41.51, -66.52) * mm});
            skLineSegment(sketch, "E59", {"start": v(-36.51, -66.52) * mm, "end": v(-38.51, -66.52) * mm});
            skLineSegment(sketch, "E60", {"start": v(-38.51, -66.52) * mm, "end": v(-38.51, -65.02) * mm});
            skLineSegment(sketch, "E61", {"start": v(-38.51, -65.02) * mm, "end": v(-41.51, -65.02) * mm});
            skLineSegment(sketch, "E62", {"start": v(-41.51, -65.02) * mm, "end": v(-41.51, -66.52) * mm});
            skLineSegment(sketch, "E63.bottom", {"start": v(-1.89, -97.57) * mm, "end": v(-15.69, -97.57) * mm});
            skLineSegment(sketch, "E63.top", {"start": v(-1.89, -83.77) * mm, "end": v(-15.69, -83.77) * mm});
            skLineSegment(sketch, "E63.left", {"start": v(-1.89, -97.57) * mm, "end": v(-1.89, -83.77) * mm});
            skLineSegment(sketch, "E63.right", {"start": v(-15.69, -97.57) * mm, "end": v(-15.69, -83.77) * mm});
            skPoint(sketch, "E63.middle", {"position": v(-8.79, -90.67) * mm});
            skPoint(sketch, "E63.middle.positionSnap0", {"position": v(4.86, -90.67) * mm});
            skPoint(sketch, "E63.middle.positionSnap1", {"position": v(-8.79, -99.7) * mm});
            skPoint(sketch, "E63.centerSnap0", {"position": v(4.86, -90.67) * mm});
            skPoint(sketch, "E63.centerSnap1", {"position": v(-8.79, -99.7) * mm});
            skLineSegment(sketch, "E64.bottom", {"start": v(36.79, -97.57) * mm, "end": v(22.99, -97.57) * mm});
            skLineSegment(sketch, "E64.top", {"start": v(36.79, -83.77) * mm, "end": v(22.99, -83.77) * mm});
            skLineSegment(sketch, "E64.left", {"start": v(36.79, -97.57) * mm, "end": v(36.79, -83.77) * mm});
            skLineSegment(sketch, "E64.right", {"start": v(22.99, -97.57) * mm, "end": v(22.99, -83.77) * mm});
            skPoint(sketch, "E64.middle", {"position": v(29.89, -90.67) * mm});
            skPoint(sketch, "E64.middle.positionSnap0", {"position": v(54.91, -90.67) * mm});
            skPoint(sketch, "E64.middle.positionSnap1", {"position": v(29.89, -99.7) * mm});
            skPoint(sketch, "E64.centerSnap0", {"position": v(54.91, -90.67) * mm});
            skPoint(sketch, "E64.centerSnap1", {"position": v(29.89, -99.7) * mm});
            skLineSegment(sketch, "E65.bottom", {"start": v(86.84, -97.57) * mm, "end": v(73.04, -97.57) * mm});
            skLineSegment(sketch, "E65.top", {"start": v(86.84, -83.77) * mm, "end": v(73.04, -83.77) * mm});
            skLineSegment(sketch, "E65.left", {"start": v(86.84, -97.57) * mm, "end": v(86.84, -83.77) * mm});
            skLineSegment(sketch, "E65.right", {"start": v(73.04, -97.57) * mm, "end": v(73.04, -83.77) * mm});
            skPoint(sketch, "E65.middle", {"position": v(79.94, -90.67) * mm});
            skPoint(sketch, "E65.middle.positionSnap0", {"position": v(104.96, -90.67) * mm});
            skPoint(sketch, "E65.middle.positionSnap1", {"position": v(79.94, -99.7) * mm});
            skPoint(sketch, "E65.centerSnap0", {"position": v(104.96, -90.67) * mm});
            skPoint(sketch, "E65.centerSnap1", {"position": v(79.94, -99.7) * mm});
            skLineSegment(sketch, "E66.bottom", {"start": v(125.51, -97.57) * mm, "end": v(111.71, -97.57) * mm});
            skLineSegment(sketch, "E66.top", {"start": v(125.51, -83.77) * mm, "end": v(111.71, -83.77) * mm});
            skLineSegment(sketch, "E66.left", {"start": v(125.51, -97.57) * mm, "end": v(125.51, -83.77) * mm});
            skLineSegment(sketch, "E66.right", {"start": v(111.71, -97.57) * mm, "end": v(111.71, -83.77) * mm});
            skPoint(sketch, "E66.middle", {"position": v(118.61, -90.67) * mm});
            skPoint(sketch, "E66.middle.positionSnap0", {"position": v(132.26, -90.67) * mm});
            skPoint(sketch, "E66.middle.positionSnap1", {"position": v(118.61, -99.7) * mm});
            skPoint(sketch, "E66.centerSnap0", {"position": v(132.26, -90.67) * mm});
            skPoint(sketch, "E66.centerSnap1", {"position": v(118.61, -99.7) * mm});
            skLineSegment(sketch, "E67.bottom", {"start": v(148.26, -97.57) * mm, "end": v(134.46, -97.57) * mm});
            skLineSegment(sketch, "E67.top", {"start": v(148.26, -83.77) * mm, "end": v(134.46, -83.77) * mm});
            skLineSegment(sketch, "E67.left", {"start": v(148.26, -97.57) * mm, "end": v(148.26, -83.77) * mm});
            skLineSegment(sketch, "E67.right", {"start": v(134.46, -97.57) * mm, "end": v(134.46, -83.77) * mm});
            skPoint(sketch, "E67.middle", {"position": v(141.36, -90.67) * mm});
            skPoint(sketch, "E67.middle.positionSnap0", {"position": v(150.46, -90.67) * mm});
            skPoint(sketch, "E67.middle.positionSnap1", {"position": v(141.36, -99.7) * mm});
            skPoint(sketch, "E67.centerSnap0", {"position": v(150.46, -90.67) * mm});
            skPoint(sketch, "E67.centerSnap1", {"position": v(141.36, -99.7) * mm});
            skLineSegment(sketch, "E68", {"start": v(-43.51, -77.52) * mm, "end": v(-36.51, -77.52) * mm});
            skLineSegment(sketch, "E69", {"start": v(29.89, -97.57) * mm, "end": v(29.89, -95.57) * mm, "construction": true});
            skLineSegment(sketch, "E70", {"start": v(29.89, -95.57) * mm, "end": v(14.39, -95.57) * mm, "construction": true});
            skLineSegment(sketch, "E71", {"start": v(29.89, -95.57) * mm, "end": v(45.39, -95.57) * mm, "construction": true});
            skLineSegment(sketch, "E72", {"start": v(14.39, -95.57) * mm, "end": v(21.39, -95.57) * mm});
            skLineSegment(sketch, "E73", {"start": v(21.39, -95.57) * mm, "end": v(21.39, -93.57) * mm});
            skLineSegment(sketch, "E74", {"start": v(21.39, -93.57) * mm, "end": v(22.99, -93.57) * mm});
            skLineSegment(sketch, "E75", {"start": v(22.99, -93.57) * mm, "end": v(22.99, -91.57) * mm});
            skLineSegment(sketch, "E76", {"start": v(22.99, -91.57) * mm, "end": v(21.39, -91.57) * mm});
            skLineSegment(sketch, "E77", {"start": v(21.39, -91.57) * mm, "end": v(21.39, -84.57) * mm});
            skLineSegment(sketch, "E78", {"start": v(14.39, -95.57) * mm, "end": v(14.39, -93.57) * mm});
            skLineSegment(sketch, "E79", {"start": v(14.39, -93.57) * mm, "end": v(12.89, -93.57) * mm});
            skLineSegment(sketch, "E80", {"start": v(12.89, -93.57) * mm, "end": v(12.89, -91.57) * mm});
            skLineSegment(sketch, "E81", {"start": v(12.89, -91.57) * mm, "end": v(14.39, -91.57) * mm});
            skLineSegment(sketch, "E82", {"start": v(14.39, -91.57) * mm, "end": v(14.39, -84.57) * mm});
            skLineSegment(sketch, "E83", {"start": v(14.39, -84.57) * mm, "end": v(16.39, -84.57) * mm});
            skLineSegment(sketch, "E84", {"start": v(21.39, -84.57) * mm, "end": v(19.39, -84.57) * mm});
            skLineSegment(sketch, "E85", {"start": v(19.39, -84.57) * mm, "end": v(19.39, -83.07) * mm});
            skLineSegment(sketch, "E86", {"start": v(19.39, -83.07) * mm, "end": v(16.39, -83.07) * mm});
            skLineSegment(sketch, "E87", {"start": v(16.39, -83.07) * mm, "end": v(16.39, -84.57) * mm});
            skLineSegment(sketch, "E88", {"start": v(45.39, -95.57) * mm, "end": v(45.39, -93.57) * mm});
            skLineSegment(sketch, "E89", {"start": v(45.39, -93.57) * mm, "end": v(46.89, -93.57) * mm});
            skLineSegment(sketch, "E90", {"start": v(46.89, -93.57) * mm, "end": v(46.89, -91.57) * mm});
            skLineSegment(sketch, "E91", {"start": v(46.89, -91.57) * mm, "end": v(45.39, -91.57) * mm});
            skLineSegment(sketch, "E92", {"start": v(45.39, -91.57) * mm, "end": v(45.39, -84.57) * mm});
            skLineSegment(sketch, "E93", {"start": v(38.39, -95.57) * mm, "end": v(38.39, -93.57) * mm});
            skLineSegment(sketch, "E94", {"start": v(38.39, -93.57) * mm, "end": v(36.79, -93.57) * mm});
            skLineSegment(sketch, "E95", {"start": v(36.79, -93.57) * mm, "end": v(36.79, -91.57) * mm});
            skLineSegment(sketch, "E96", {"start": v(36.79, -91.57) * mm, "end": v(38.39, -91.57) * mm});
            skLineSegment(sketch, "E97", {"start": v(38.39, -91.57) * mm, "end": v(38.39, -84.57) * mm});
            skLineSegment(sketch, "E98", {"start": v(38.39, -84.57) * mm, "end": v(40.39, -84.57) * mm});
            skLineSegment(sketch, "E99", {"start": v(45.39, -84.57) * mm, "end": v(43.39, -84.57) * mm});
            skLineSegment(sketch, "E100", {"start": v(43.39, -84.57) * mm, "end": v(43.39, -83.07) * mm});
            skLineSegment(sketch, "E101", {"start": v(43.39, -83.07) * mm, "end": v(40.39, -83.07) * mm});
            skLineSegment(sketch, "E102", {"start": v(40.39, -83.07) * mm, "end": v(40.39, -84.57) * mm});
            skLineSegment(sketch, "E103", {"start": v(38.39, -95.57) * mm, "end": v(45.39, -95.57) * mm});
            skLineSegment(sketch, "E104", {"start": v(79.94, -97.57) * mm, "end": v(79.94, -95.57) * mm, "construction": true});
            skLineSegment(sketch, "E105", {"start": v(79.94, -95.57) * mm, "end": v(64.44, -95.57) * mm, "construction": true});
            skLineSegment(sketch, "E106", {"start": v(79.94, -95.57) * mm, "end": v(95.44, -95.57) * mm, "construction": true});
            skLineSegment(sketch, "E107", {"start": v(64.44, -95.57) * mm, "end": v(71.44, -95.57) * mm});
            skLineSegment(sketch, "E108", {"start": v(71.44, -95.57) * mm, "end": v(71.44, -93.57) * mm});
            skLineSegment(sketch, "E109", {"start": v(71.44, -93.57) * mm, "end": v(73.04, -93.57) * mm});
            skLineSegment(sketch, "E110", {"start": v(73.04, -93.57) * mm, "end": v(73.04, -91.57) * mm});
            skLineSegment(sketch, "E111", {"start": v(73.04, -91.57) * mm, "end": v(71.44, -91.57) * mm});
            skLineSegment(sketch, "E112", {"start": v(71.44, -91.57) * mm, "end": v(71.44, -84.57) * mm});
            skLineSegment(sketch, "E113", {"start": v(64.44, -95.57) * mm, "end": v(64.44, -93.57) * mm});
            skLineSegment(sketch, "E114", {"start": v(64.44, -93.57) * mm, "end": v(62.94, -93.57) * mm});
            skLineSegment(sketch, "E115", {"start": v(62.94, -93.57) * mm, "end": v(62.94, -91.57) * mm});
            skLineSegment(sketch, "E116", {"start": v(62.94, -91.57) * mm, "end": v(64.44, -91.57) * mm});
            skLineSegment(sketch, "E117", {"start": v(64.44, -91.57) * mm, "end": v(64.44, -84.57) * mm});
            skLineSegment(sketch, "E118", {"start": v(64.44, -84.57) * mm, "end": v(66.44, -84.57) * mm});
            skLineSegment(sketch, "E119", {"start": v(71.44, -84.57) * mm, "end": v(69.44, -84.57) * mm});
            skLineSegment(sketch, "E120", {"start": v(69.44, -84.57) * mm, "end": v(69.44, -83.07) * mm});
            skLineSegment(sketch, "E121", {"start": v(69.44, -83.07) * mm, "end": v(66.44, -83.07) * mm});
            skLineSegment(sketch, "E122", {"start": v(66.44, -83.07) * mm, "end": v(66.44, -84.57) * mm});
            skLineSegment(sketch, "E123", {"start": v(95.44, -95.57) * mm, "end": v(95.44, -93.57) * mm});
            skLineSegment(sketch, "E124", {"start": v(95.44, -93.57) * mm, "end": v(96.94, -93.57) * mm});
            skLineSegment(sketch, "E125", {"start": v(96.94, -93.57) * mm, "end": v(96.94, -91.57) * mm});
            skLineSegment(sketch, "E126", {"start": v(96.94, -91.57) * mm, "end": v(95.44, -91.57) * mm});
            skLineSegment(sketch, "E127", {"start": v(95.44, -91.57) * mm, "end": v(95.44, -84.57) * mm});
            skLineSegment(sketch, "E128", {"start": v(88.44, -95.57) * mm, "end": v(88.44, -93.57) * mm});
            skLineSegment(sketch, "E129", {"start": v(88.44, -93.57) * mm, "end": v(86.84, -93.57) * mm});
            skLineSegment(sketch, "E130", {"start": v(86.84, -93.57) * mm, "end": v(86.84, -91.57) * mm});
            skLineSegment(sketch, "E131", {"start": v(86.84, -91.57) * mm, "end": v(88.44, -91.57) * mm});
            skLineSegment(sketch, "E132", {"start": v(88.44, -91.57) * mm, "end": v(88.44, -84.57) * mm});
            skLineSegment(sketch, "E133", {"start": v(88.44, -84.57) * mm, "end": v(90.44, -84.57) * mm});
            skLineSegment(sketch, "E134", {"start": v(95.44, -84.57) * mm, "end": v(93.44, -84.57) * mm});
            skLineSegment(sketch, "E135", {"start": v(93.44, -84.57) * mm, "end": v(93.44, -83.07) * mm});
            skLineSegment(sketch, "E136", {"start": v(93.44, -83.07) * mm, "end": v(90.44, -83.07) * mm});
            skLineSegment(sketch, "E137", {"start": v(90.44, -83.07) * mm, "end": v(90.44, -84.57) * mm});
            skLineSegment(sketch, "E138", {"start": v(88.44, -95.57) * mm, "end": v(95.44, -95.57) * mm});
            skLineSegment(sketch, "E139.bottom", {"start": v(186.94, -61.47) * mm, "end": v(173.14, -61.47) * mm});
            skLineSegment(sketch, "E139.top", {"start": v(186.94, -47.67) * mm, "end": v(173.14, -47.67) * mm});
            skLineSegment(sketch, "E139.left", {"start": v(186.94, -61.47) * mm, "end": v(186.94, -47.67) * mm});
            skLineSegment(sketch, "E139.right", {"start": v(173.14, -61.47) * mm, "end": v(173.14, -47.67) * mm});
            skPoint(sketch, "E139.middle", {"position": v(180.04, -54.57) * mm});
            skPoint(sketch, "E139.middle.positionSnap0", {"position": v(180.04, -63.6) * mm});
            skPoint(sketch, "E139.middle.positionSnap1", {"position": v(159.56, -54.57) * mm});
            skPoint(sketch, "E139.centerSnap0", {"position": v(180.04, -63.6) * mm});
            skPoint(sketch, "E139.centerSnap1", {"position": v(159.56, -54.57) * mm});
            skLineSegment(sketch, "E140.bottom", {"start": v(193.76, -43.42) * mm, "end": v(179.96, -43.42) * mm});
            skLineSegment(sketch, "E140.top", {"start": v(193.76, -29.62) * mm, "end": v(179.96, -29.62) * mm});
            skLineSegment(sketch, "E140.left", {"start": v(193.76, -43.42) * mm, "end": v(193.76, -29.62) * mm});
            skLineSegment(sketch, "E140.right", {"start": v(179.96, -43.42) * mm, "end": v(179.96, -29.62) * mm});
            skPoint(sketch, "E140.middle", {"position": v(186.86, -36.52) * mm});
            skPoint(sketch, "E140.middle.positionSnap0", {"position": v(173.21, -36.52) * mm});
            skPoint(sketch, "E140.middle.positionSnap1", {"position": v(186.86, -45.55) * mm});
            skPoint(sketch, "E140.centerSnap0", {"position": v(173.21, -36.52) * mm});
            skPoint(sketch, "E140.centerSnap1", {"position": v(186.86, -45.55) * mm});
            skLineSegment(sketch, "E141.bottom", {"start": v(173.29, -79.52) * mm, "end": v(159.49, -79.52) * mm});
            skLineSegment(sketch, "E141.top", {"start": v(173.29, -65.72) * mm, "end": v(159.49, -65.72) * mm});
            skLineSegment(sketch, "E141.left", {"start": v(173.29, -79.52) * mm, "end": v(173.29, -65.72) * mm});
            skLineSegment(sketch, "E141.right", {"start": v(159.49, -79.52) * mm, "end": v(159.49, -65.72) * mm});
            skPoint(sketch, "E141.middle", {"position": v(166.39, -72.62) * mm});
            skPoint(sketch, "E141.middle.positionSnap0", {"position": v(150.46, -72.62) * mm});
            skPoint(sketch, "E141.middle.positionSnap1", {"position": v(166.39, -81.65) * mm});
            skPoint(sketch, "E141.centerSnap0", {"position": v(150.46, -72.62) * mm});
            skPoint(sketch, "E141.centerSnap1", {"position": v(166.39, -81.65) * mm});
            skLineSegment(sketch, "E142.bottom", {"start": v(198.31, -79.52) * mm, "end": v(184.51, -79.52) * mm});
            skLineSegment(sketch, "E142.top", {"start": v(198.31, -65.72) * mm, "end": v(184.51, -65.72) * mm});
            skLineSegment(sketch, "E142.left", {"start": v(198.31, -79.52) * mm, "end": v(198.31, -65.72) * mm});
            skLineSegment(sketch, "E142.right", {"start": v(184.51, -79.52) * mm, "end": v(184.51, -65.72) * mm});
            skPoint(sketch, "E142.middle", {"position": v(191.41, -72.62) * mm});
            skPoint(sketch, "E142.middle.positionSnap0", {"position": v(182.31, -72.62) * mm});
            skPoint(sketch, "E142.middle.positionSnap1", {"position": v(191.41, -81.65) * mm});
            skPoint(sketch, "E142.centerSnap0", {"position": v(182.31, -72.62) * mm});
            skPoint(sketch, "E142.centerSnap1", {"position": v(191.41, -81.65) * mm});
            skLineSegment(sketch, "E143.1.0.0", {"start": v(-38.29, -11.57) * mm, "end": v(-52.09, -11.57) * mm});
            skLineSegment(sketch, "E143.1.0.1", {"start": v(-38.29, -11.57) * mm, "end": v(-38.29, -25.37) * mm});
            skLineSegment(sketch, "E143.1.0.2", {"start": v(-38.29, -25.37) * mm, "end": v(-52.09, -25.37) * mm});
            skLineSegment(sketch, "E143.1.0.3", {"start": v(-52.09, -11.57) * mm, "end": v(-52.09, -25.37) * mm});
            skLineSegment(sketch, "E143.2.0.0", {"start": v(-20.09, -11.57) * mm, "end": v(-33.89, -11.57) * mm});
            skLineSegment(sketch, "E143.2.0.1", {"start": v(-20.09, -11.57) * mm, "end": v(-20.09, -25.37) * mm});
            skLineSegment(sketch, "E143.2.0.2", {"start": v(-20.09, -25.37) * mm, "end": v(-33.89, -25.37) * mm});
            skLineSegment(sketch, "E143.2.0.3", {"start": v(-33.89, -11.57) * mm, "end": v(-33.89, -25.37) * mm});
            skLineSegment(sketch, "E143.3.0.0", {"start": v(-1.89, -11.57) * mm, "end": v(-15.69, -11.57) * mm});
            skLineSegment(sketch, "E143.3.0.1", {"start": v(-1.89, -11.57) * mm, "end": v(-1.89, -25.37) * mm});
            skLineSegment(sketch, "E143.3.0.2", {"start": v(-1.89, -25.37) * mm, "end": v(-15.69, -25.37) * mm});
            skLineSegment(sketch, "E143.3.0.3", {"start": v(-15.69, -11.57) * mm, "end": v(-15.69, -25.37) * mm});
            skLineSegment(sketch, "E143.4.0.0", {"start": v(16.31, -11.57) * mm, "end": v(2.51, -11.57) * mm});
            skLineSegment(sketch, "E143.4.0.1", {"start": v(16.31, -11.57) * mm, "end": v(16.31, -25.37) * mm});
            skLineSegment(sketch, "E143.4.0.2", {"start": v(16.31, -25.37) * mm, "end": v(2.51, -25.37) * mm});
            skLineSegment(sketch, "E143.4.0.3", {"start": v(2.51, -11.57) * mm, "end": v(2.51, -25.37) * mm});
            skLineSegment(sketch, "E143.5.0.0", {"start": v(34.51, -11.57) * mm, "end": v(20.71, -11.57) * mm});
            skLineSegment(sketch, "E143.5.0.1", {"start": v(34.51, -11.57) * mm, "end": v(34.51, -25.37) * mm});
            skLineSegment(sketch, "E143.5.0.2", {"start": v(34.51, -25.37) * mm, "end": v(20.71, -25.37) * mm});
            skLineSegment(sketch, "E143.5.0.3", {"start": v(20.71, -11.57) * mm, "end": v(20.71, -25.37) * mm});
            skLineSegment(sketch, "E143.6.0.0", {"start": v(52.71, -11.57) * mm, "end": v(38.91, -11.57) * mm});
            skLineSegment(sketch, "E143.6.0.1", {"start": v(52.71, -11.57) * mm, "end": v(52.71, -25.37) * mm});
            skLineSegment(sketch, "E143.6.0.2", {"start": v(52.71, -25.37) * mm, "end": v(38.91, -25.37) * mm});
            skLineSegment(sketch, "E143.6.0.3", {"start": v(38.91, -11.57) * mm, "end": v(38.91, -25.37) * mm});
            skLineSegment(sketch, "E143.7.0.0", {"start": v(70.91, -11.57) * mm, "end": v(57.11, -11.57) * mm});
            skLineSegment(sketch, "E143.7.0.1", {"start": v(70.91, -11.57) * mm, "end": v(70.91, -25.37) * mm});
            skLineSegment(sketch, "E143.7.0.2", {"start": v(70.91, -25.37) * mm, "end": v(57.11, -25.37) * mm});
            skLineSegment(sketch, "E143.7.0.3", {"start": v(57.11, -11.57) * mm, "end": v(57.11, -25.37) * mm});
            skLineSegment(sketch, "E143.8.0.0", {"start": v(89.11, -11.57) * mm, "end": v(75.31, -11.57) * mm});
            skLineSegment(sketch, "E143.8.0.1", {"start": v(89.11, -11.57) * mm, "end": v(89.11, -25.37) * mm});
            skLineSegment(sketch, "E143.8.0.2", {"start": v(89.11, -25.37) * mm, "end": v(75.31, -25.37) * mm});
            skLineSegment(sketch, "E143.8.0.3", {"start": v(75.31, -11.57) * mm, "end": v(75.31, -25.37) * mm});
            skLineSegment(sketch, "E143.9.0.0", {"start": v(107.31, -11.57) * mm, "end": v(93.51, -11.57) * mm});
            skLineSegment(sketch, "E143.9.0.1", {"start": v(107.31, -11.57) * mm, "end": v(107.31, -25.37) * mm});
            skLineSegment(sketch, "E143.9.0.2", {"start": v(107.31, -25.37) * mm, "end": v(93.51, -25.37) * mm});
            skLineSegment(sketch, "E143.9.0.3", {"start": v(93.51, -11.57) * mm, "end": v(93.51, -25.37) * mm});
            skLineSegment(sketch, "E143.10.0.0", {"start": v(125.51, -11.57) * mm, "end": v(111.71, -11.57) * mm});
            skLineSegment(sketch, "E143.10.0.1", {"start": v(125.51, -11.57) * mm, "end": v(125.51, -25.37) * mm});
            skLineSegment(sketch, "E143.10.0.2", {"start": v(125.51, -25.37) * mm, "end": v(111.71, -25.37) * mm});
            skLineSegment(sketch, "E143.10.0.3", {"start": v(111.71, -11.57) * mm, "end": v(111.71, -25.37) * mm});
            skLineSegment(sketch, "E143.11.0.0", {"start": v(143.71, -11.57) * mm, "end": v(129.91, -11.57) * mm});
            skLineSegment(sketch, "E143.11.0.1", {"start": v(143.71, -11.57) * mm, "end": v(143.71, -25.37) * mm});
            skLineSegment(sketch, "E143.11.0.2", {"start": v(143.71, -25.37) * mm, "end": v(129.91, -25.37) * mm});
            skLineSegment(sketch, "E143.11.0.3", {"start": v(129.91, -11.57) * mm, "end": v(129.91, -25.37) * mm});
            skLineSegment(sketch, "E143.12.0.0", {"start": v(161.91, -11.57) * mm, "end": v(148.11, -11.57) * mm});
            skLineSegment(sketch, "E143.12.0.1", {"start": v(161.91, -11.57) * mm, "end": v(161.91, -25.37) * mm});
            skLineSegment(sketch, "E143.12.0.2", {"start": v(161.91, -25.37) * mm, "end": v(148.11, -25.37) * mm});
            skLineSegment(sketch, "E143.12.0.3", {"start": v(148.11, -11.57) * mm, "end": v(148.11, -25.37) * mm});
            skLineSegment(sketch, "E143.13.0.0", {"start": v(180.11, -11.57) * mm, "end": v(166.31, -11.57) * mm});
            skLineSegment(sketch, "E143.13.0.1", {"start": v(180.11, -11.57) * mm, "end": v(180.11, -25.37) * mm});
            skLineSegment(sketch, "E143.13.0.2", {"start": v(180.11, -25.37) * mm, "end": v(166.31, -25.37) * mm});
            skLineSegment(sketch, "E143.13.0.3", {"start": v(166.31, -11.57) * mm, "end": v(166.31, -25.37) * mm});
            skLineSegment(sketch, "E143.14.0.0", {"start": v(198.31, -11.57) * mm, "end": v(184.51, -11.57) * mm});
            skLineSegment(sketch, "E143.14.0.1", {"start": v(198.31, -11.57) * mm, "end": v(198.31, -25.37) * mm});
            skLineSegment(sketch, "E143.14.0.2", {"start": v(198.31, -25.37) * mm, "end": v(184.51, -25.37) * mm});
            skLineSegment(sketch, "E143.14.0.3", {"start": v(184.51, -11.57) * mm, "end": v(184.51, -25.37) * mm});
            skLineSegment(sketch, "E143.direction1", {"start": v(-70.29, -25.37) * mm, "end": v(-52.09, -25.37) * mm, "construction": true});
            skLineSegment(sketch, "E144.bottom", {"start": v(-29.19, -43.42) * mm, "end": v(-42.99, -43.42) * mm});
            skLineSegment(sketch, "E144.top", {"start": v(-29.19, -29.62) * mm, "end": v(-42.99, -29.62) * mm});
            skLineSegment(sketch, "E144.left", {"start": v(-29.19, -43.42) * mm, "end": v(-29.19, -29.62) * mm});
            skLineSegment(sketch, "E144.right", {"start": v(-42.99, -43.42) * mm, "end": v(-42.99, -29.62) * mm});
            skPoint(sketch, "E144.middle", {"position": v(-36.09, -36.52) * mm});
            skPoint(sketch, "E144.middle.positionSnap0", {"position": v(-36.09, -45.55) * mm});
            skPoint(sketch, "E144.middle.positionSnap1", {"position": v(-45.19, -36.52) * mm});
            skPoint(sketch, "E144.centerSnap0", {"position": v(-36.09, -45.55) * mm});
            skPoint(sketch, "E144.centerSnap1", {"position": v(-45.19, -36.52) * mm});
            skLineSegment(sketch, "E145.bottom", {"start": v(-24.64, -61.47) * mm, "end": v(-38.44, -61.47) * mm});
            skLineSegment(sketch, "E145.top", {"start": v(-24.64, -47.67) * mm, "end": v(-38.44, -47.67) * mm});
            skLineSegment(sketch, "E145.left", {"start": v(-24.64, -61.47) * mm, "end": v(-24.64, -47.67) * mm});
            skLineSegment(sketch, "E145.right", {"start": v(-38.44, -61.47) * mm, "end": v(-38.44, -47.67) * mm});
            skPoint(sketch, "E145.middle", {"position": v(-31.54, -54.57) * mm});
            skPoint(sketch, "E145.middle.positionSnap0", {"position": v(-40.64, -54.57) * mm});
            skPoint(sketch, "E145.centerSnap0", {"position": v(-40.64, -54.57) * mm});
            skLineSegment(sketch, "E146.bottom", {"start": v(-15.54, -79.52) * mm, "end": v(-29.34, -79.52) * mm});
            skLineSegment(sketch, "E146.top", {"start": v(-15.54, -65.72) * mm, "end": v(-29.34, -65.72) * mm});
            skLineSegment(sketch, "E146.left", {"start": v(-15.54, -79.52) * mm, "end": v(-15.54, -65.72) * mm});
            skLineSegment(sketch, "E146.right", {"start": v(-29.34, -79.52) * mm, "end": v(-29.34, -65.72) * mm});
            skPoint(sketch, "E146.middle", {"position": v(-22.44, -72.62) * mm});
            skPoint(sketch, "E146.middle.positionSnap0", {"position": v(-31.54, -72.62) * mm});
            skPoint(sketch, "E146.centerSnap0", {"position": v(-31.54, -72.62) * mm});
            skLineSegment(sketch, "E147.1.0.0", {"start": v(-10.99, -43.42) * mm, "end": v(-24.79, -43.42) * mm});
            skLineSegment(sketch, "E147.1.0.1", {"start": v(-24.79, -43.42) * mm, "end": v(-24.79, -29.62) * mm});
            skLineSegment(sketch, "E147.1.0.2", {"start": v(-10.99, -29.62) * mm, "end": v(-24.79, -29.62) * mm});
            skLineSegment(sketch, "E147.1.0.3", {"start": v(-10.99, -43.42) * mm, "end": v(-10.99, -29.62) * mm});
            skPoint(sketch, "E147.1.0.4", {"position": v(-17.89, -36.52) * mm});
            skLineSegment(sketch, "E147.2.0.0", {"start": v(7.21, -43.42) * mm, "end": v(-6.59, -43.42) * mm});
            skLineSegment(sketch, "E147.2.0.1", {"start": v(-6.59, -43.42) * mm, "end": v(-6.59, -29.62) * mm});
            skLineSegment(sketch, "E147.2.0.2", {"start": v(7.21, -29.62) * mm, "end": v(-6.59, -29.62) * mm});
            skLineSegment(sketch, "E147.2.0.3", {"start": v(7.21, -43.42) * mm, "end": v(7.21, -29.62) * mm});
            skPoint(sketch, "E147.2.0.4", {"position": v(0.31, -36.52) * mm});
            skLineSegment(sketch, "E147.3.0.0", {"start": v(25.41, -43.42) * mm, "end": v(11.61, -43.42) * mm});
            skLineSegment(sketch, "E147.3.0.1", {"start": v(11.61, -43.42) * mm, "end": v(11.61, -29.62) * mm});
            skLineSegment(sketch, "E147.3.0.2", {"start": v(25.41, -29.62) * mm, "end": v(11.61, -29.62) * mm});
            skLineSegment(sketch, "E147.3.0.3", {"start": v(25.41, -43.42) * mm, "end": v(25.41, -29.62) * mm});
            skPoint(sketch, "E147.3.0.4", {"position": v(18.51, -36.52) * mm});
            skLineSegment(sketch, "E147.4.0.0", {"start": v(43.61, -43.42) * mm, "end": v(29.81, -43.42) * mm});
            skLineSegment(sketch, "E147.4.0.1", {"start": v(29.81, -43.42) * mm, "end": v(29.81, -29.62) * mm});
            skLineSegment(sketch, "E147.4.0.2", {"start": v(43.61, -29.62) * mm, "end": v(29.81, -29.62) * mm});
            skLineSegment(sketch, "E147.4.0.3", {"start": v(43.61, -43.42) * mm, "end": v(43.61, -29.62) * mm});
            skPoint(sketch, "E147.4.0.4", {"position": v(36.71, -36.52) * mm});
            skLineSegment(sketch, "E147.5.0.0", {"start": v(61.81, -43.42) * mm, "end": v(48.01, -43.42) * mm});
            skLineSegment(sketch, "E147.5.0.1", {"start": v(48.01, -43.42) * mm, "end": v(48.01, -29.62) * mm});
            skLineSegment(sketch, "E147.5.0.2", {"start": v(61.81, -29.62) * mm, "end": v(48.01, -29.62) * mm});
            skLineSegment(sketch, "E147.5.0.3", {"start": v(61.81, -43.42) * mm, "end": v(61.81, -29.62) * mm});
            skPoint(sketch, "E147.5.0.4", {"position": v(54.91, -36.52) * mm});
            skLineSegment(sketch, "E147.6.0.0", {"start": v(80.01, -43.42) * mm, "end": v(66.21, -43.42) * mm});
            skLineSegment(sketch, "E147.6.0.1", {"start": v(66.21, -43.42) * mm, "end": v(66.21, -29.62) * mm});
            skLineSegment(sketch, "E147.6.0.2", {"start": v(80.01, -29.62) * mm, "end": v(66.21, -29.62) * mm});
            skLineSegment(sketch, "E147.6.0.3", {"start": v(80.01, -43.42) * mm, "end": v(80.01, -29.62) * mm});
            skPoint(sketch, "E147.6.0.4", {"position": v(73.11, -36.52) * mm});
            skLineSegment(sketch, "E147.7.0.0", {"start": v(98.21, -43.42) * mm, "end": v(84.41, -43.42) * mm});
            skLineSegment(sketch, "E147.7.0.1", {"start": v(84.41, -43.42) * mm, "end": v(84.41, -29.62) * mm});
            skLineSegment(sketch, "E147.7.0.2", {"start": v(98.21, -29.62) * mm, "end": v(84.41, -29.62) * mm});
            skLineSegment(sketch, "E147.7.0.3", {"start": v(98.21, -43.42) * mm, "end": v(98.21, -29.62) * mm});
            skPoint(sketch, "E147.7.0.4", {"position": v(91.31, -36.52) * mm});
            skLineSegment(sketch, "E147.8.0.0", {"start": v(116.41, -43.42) * mm, "end": v(102.61, -43.42) * mm});
            skLineSegment(sketch, "E147.8.0.1", {"start": v(102.61, -43.42) * mm, "end": v(102.61, -29.62) * mm});
            skLineSegment(sketch, "E147.8.0.2", {"start": v(116.41, -29.62) * mm, "end": v(102.61, -29.62) * mm});
            skLineSegment(sketch, "E147.8.0.3", {"start": v(116.41, -43.42) * mm, "end": v(116.41, -29.62) * mm});
            skPoint(sketch, "E147.8.0.4", {"position": v(109.51, -36.52) * mm});
            skLineSegment(sketch, "E147.9.0.0", {"start": v(134.61, -43.42) * mm, "end": v(120.81, -43.42) * mm});
            skLineSegment(sketch, "E147.9.0.1", {"start": v(120.81, -43.42) * mm, "end": v(120.81, -29.62) * mm});
            skLineSegment(sketch, "E147.9.0.2", {"start": v(134.61, -29.62) * mm, "end": v(120.81, -29.62) * mm});
            skLineSegment(sketch, "E147.9.0.3", {"start": v(134.61, -43.42) * mm, "end": v(134.61, -29.62) * mm});
            skPoint(sketch, "E147.9.0.4", {"position": v(127.71, -36.52) * mm});
            skLineSegment(sketch, "E147.10.0.0", {"start": v(152.81, -43.42) * mm, "end": v(139.01, -43.42) * mm});
            skLineSegment(sketch, "E147.10.0.1", {"start": v(139.01, -43.42) * mm, "end": v(139.01, -29.62) * mm});
            skLineSegment(sketch, "E147.10.0.2", {"start": v(152.81, -29.62) * mm, "end": v(139.01, -29.62) * mm});
            skLineSegment(sketch, "E147.10.0.3", {"start": v(152.81, -43.42) * mm, "end": v(152.81, -29.62) * mm});
            skPoint(sketch, "E147.10.0.4", {"position": v(145.91, -36.52) * mm});
            skLineSegment(sketch, "E147.11.0.0", {"start": v(171.01, -43.42) * mm, "end": v(157.21, -43.42) * mm});
            skLineSegment(sketch, "E147.11.0.1", {"start": v(157.21, -43.42) * mm, "end": v(157.21, -29.62) * mm});
            skLineSegment(sketch, "E147.11.0.2", {"start": v(171.01, -29.62) * mm, "end": v(157.21, -29.62) * mm});
            skLineSegment(sketch, "E147.11.0.3", {"start": v(171.01, -43.42) * mm, "end": v(171.01, -29.62) * mm});
            skPoint(sketch, "E147.11.0.4", {"position": v(164.11, -36.52) * mm});
            skLineSegment(sketch, "E147.direction1", {"start": v(-42.99, -43.42) * mm, "end": v(-24.79, -43.42) * mm, "construction": true});
            skPoint(sketch, "E148.1.0.0", {"position": v(-13.34, -54.57) * mm});
            skLineSegment(sketch, "E148.1.0.1", {"start": v(-6.44, -61.47) * mm, "end": v(-20.24, -61.47) * mm});
            skLineSegment(sketch, "E148.1.0.2", {"start": v(-6.44, -61.47) * mm, "end": v(-6.44, -47.67) * mm});
            skLineSegment(sketch, "E148.1.0.3", {"start": v(-20.24, -61.47) * mm, "end": v(-20.24, -47.67) * mm});
            skLineSegment(sketch, "E148.1.0.4", {"start": v(-6.44, -47.67) * mm, "end": v(-20.24, -47.67) * mm});
            skPoint(sketch, "E148.1.0.5", {"position": v(-17.89, -45.55) * mm});
            skPoint(sketch, "E148.1.0.6", {"position": v(-17.89, -45.55) * mm});
            skPoint(sketch, "E148.2.0.0", {"position": v(4.86, -54.57) * mm});
            skLineSegment(sketch, "E148.2.0.1", {"start": v(11.76, -61.47) * mm, "end": v(-2.04, -61.47) * mm});
            skLineSegment(sketch, "E148.2.0.2", {"start": v(11.76, -61.47) * mm, "end": v(11.76, -47.67) * mm});
            skLineSegment(sketch, "E148.2.0.3", {"start": v(-2.04, -61.47) * mm, "end": v(-2.04, -47.67) * mm});
            skLineSegment(sketch, "E148.2.0.4", {"start": v(11.76, -47.67) * mm, "end": v(-2.04, -47.67) * mm});
            skPoint(sketch, "E148.2.0.5", {"position": v(0.31, -45.55) * mm});
            skPoint(sketch, "E148.2.0.6", {"position": v(0.31, -45.55) * mm});
            skPoint(sketch, "E148.3.0.0", {"position": v(23.06, -54.57) * mm});
            skLineSegment(sketch, "E148.3.0.1", {"start": v(29.96, -61.47) * mm, "end": v(16.16, -61.47) * mm});
            skLineSegment(sketch, "E148.3.0.2", {"start": v(29.96, -61.47) * mm, "end": v(29.96, -47.67) * mm});
            skLineSegment(sketch, "E148.3.0.3", {"start": v(16.16, -61.47) * mm, "end": v(16.16, -47.67) * mm});
            skLineSegment(sketch, "E148.3.0.4", {"start": v(29.96, -47.67) * mm, "end": v(16.16, -47.67) * mm});
            skPoint(sketch, "E148.3.0.5", {"position": v(18.51, -45.55) * mm});
            skPoint(sketch, "E148.3.0.6", {"position": v(18.51, -45.55) * mm});
            skPoint(sketch, "E148.4.0.0", {"position": v(41.26, -54.57) * mm});
            skLineSegment(sketch, "E148.4.0.1", {"start": v(48.16, -61.47) * mm, "end": v(34.36, -61.47) * mm});
            skLineSegment(sketch, "E148.4.0.2", {"start": v(48.16, -61.47) * mm, "end": v(48.16, -47.67) * mm});
            skLineSegment(sketch, "E148.4.0.3", {"start": v(34.36, -61.47) * mm, "end": v(34.36, -47.67) * mm});
            skLineSegment(sketch, "E148.4.0.4", {"start": v(48.16, -47.67) * mm, "end": v(34.36, -47.67) * mm});
            skPoint(sketch, "E148.4.0.5", {"position": v(36.71, -45.55) * mm});
            skPoint(sketch, "E148.4.0.6", {"position": v(36.71, -45.55) * mm});
            skPoint(sketch, "E148.5.0.0", {"position": v(59.46, -54.57) * mm});
            skLineSegment(sketch, "E148.5.0.1", {"start": v(66.36, -61.47) * mm, "end": v(52.56, -61.47) * mm});
            skLineSegment(sketch, "E148.5.0.2", {"start": v(66.36, -61.47) * mm, "end": v(66.36, -47.67) * mm});
            skLineSegment(sketch, "E148.5.0.3", {"start": v(52.56, -61.47) * mm, "end": v(52.56, -47.67) * mm});
            skLineSegment(sketch, "E148.5.0.4", {"start": v(66.36, -47.67) * mm, "end": v(52.56, -47.67) * mm});
            skPoint(sketch, "E148.5.0.5", {"position": v(54.91, -45.55) * mm});
            skPoint(sketch, "E148.5.0.6", {"position": v(54.91, -45.55) * mm});
            skPoint(sketch, "E148.6.0.0", {"position": v(77.66, -54.57) * mm});
            skLineSegment(sketch, "E148.6.0.1", {"start": v(84.56, -61.47) * mm, "end": v(70.76, -61.47) * mm});
            skLineSegment(sketch, "E148.6.0.2", {"start": v(84.56, -61.47) * mm, "end": v(84.56, -47.67) * mm});
            skLineSegment(sketch, "E148.6.0.3", {"start": v(70.76, -61.47) * mm, "end": v(70.76, -47.67) * mm});
            skLineSegment(sketch, "E148.6.0.4", {"start": v(84.56, -47.67) * mm, "end": v(70.76, -47.67) * mm});
            skPoint(sketch, "E148.6.0.5", {"position": v(73.11, -45.55) * mm});
            skPoint(sketch, "E148.6.0.6", {"position": v(73.11, -45.55) * mm});
            skPoint(sketch, "E148.7.0.0", {"position": v(95.86, -54.57) * mm});
            skLineSegment(sketch, "E148.7.0.1", {"start": v(102.76, -61.47) * mm, "end": v(88.96, -61.47) * mm});
            skLineSegment(sketch, "E148.7.0.2", {"start": v(102.76, -61.47) * mm, "end": v(102.76, -47.67) * mm});
            skLineSegment(sketch, "E148.7.0.3", {"start": v(88.96, -61.47) * mm, "end": v(88.96, -47.67) * mm});
            skLineSegment(sketch, "E148.7.0.4", {"start": v(102.76, -47.67) * mm, "end": v(88.96, -47.67) * mm});
            skPoint(sketch, "E148.7.0.5", {"position": v(91.31, -45.55) * mm});
            skPoint(sketch, "E148.7.0.6", {"position": v(91.31, -45.55) * mm});
            skPoint(sketch, "E148.8.0.0", {"position": v(114.06, -54.57) * mm});
            skLineSegment(sketch, "E148.8.0.1", {"start": v(120.96, -61.47) * mm, "end": v(107.16, -61.47) * mm});
            skLineSegment(sketch, "E148.8.0.2", {"start": v(120.96, -61.47) * mm, "end": v(120.96, -47.67) * mm});
            skLineSegment(sketch, "E148.8.0.3", {"start": v(107.16, -61.47) * mm, "end": v(107.16, -47.67) * mm});
            skLineSegment(sketch, "E148.8.0.4", {"start": v(120.96, -47.67) * mm, "end": v(107.16, -47.67) * mm});
            skPoint(sketch, "E148.8.0.5", {"position": v(109.51, -45.55) * mm});
            skPoint(sketch, "E148.8.0.6", {"position": v(109.51, -45.55) * mm});
            skPoint(sketch, "E148.9.0.0", {"position": v(132.26, -54.57) * mm});
            skLineSegment(sketch, "E148.9.0.1", {"start": v(139.16, -61.47) * mm, "end": v(125.36, -61.47) * mm});
            skLineSegment(sketch, "E148.9.0.2", {"start": v(139.16, -61.47) * mm, "end": v(139.16, -47.67) * mm});
            skLineSegment(sketch, "E148.9.0.3", {"start": v(125.36, -61.47) * mm, "end": v(125.36, -47.67) * mm});
            skLineSegment(sketch, "E148.9.0.4", {"start": v(139.16, -47.67) * mm, "end": v(125.36, -47.67) * mm});
            skPoint(sketch, "E148.9.0.5", {"position": v(127.71, -45.55) * mm});
            skPoint(sketch, "E148.9.0.6", {"position": v(127.71, -45.55) * mm});
            skPoint(sketch, "E148.10.0.0", {"position": v(150.46, -54.57) * mm});
            skLineSegment(sketch, "E148.10.0.1", {"start": v(157.36, -61.47) * mm, "end": v(143.56, -61.47) * mm});
            skLineSegment(sketch, "E148.10.0.2", {"start": v(157.36, -61.47) * mm, "end": v(157.36, -47.67) * mm});
            skLineSegment(sketch, "E148.10.0.3", {"start": v(143.56, -61.47) * mm, "end": v(143.56, -47.67) * mm});
            skLineSegment(sketch, "E148.10.0.4", {"start": v(157.36, -47.67) * mm, "end": v(143.56, -47.67) * mm});
            skPoint(sketch, "E148.10.0.5", {"position": v(145.91, -45.55) * mm});
            skPoint(sketch, "E148.10.0.6", {"position": v(145.91, -45.55) * mm});
            skLineSegment(sketch, "E148.direction1", {"start": v(-38.44, -61.47) * mm, "end": v(-20.24, -61.47) * mm, "construction": true});
            skLineSegment(sketch, "E149.1.0.0", {"start": v(2.66, -65.72) * mm, "end": v(-11.14, -65.72) * mm});
            skPoint(sketch, "E149.1.0.1", {"position": v(-4.24, -72.62) * mm});
            skLineSegment(sketch, "E149.1.0.2", {"start": v(2.66, -79.52) * mm, "end": v(-11.14, -79.52) * mm});
            skLineSegment(sketch, "E149.1.0.3", {"start": v(-11.14, -79.52) * mm, "end": v(-11.14, -65.72) * mm});
            skLineSegment(sketch, "E149.1.0.4", {"start": v(2.66, -79.52) * mm, "end": v(2.66, -65.72) * mm});
            skLineSegment(sketch, "E149.2.0.0", {"start": v(20.86, -65.72) * mm, "end": v(7.06, -65.72) * mm});
            skPoint(sketch, "E149.2.0.1", {"position": v(13.96, -72.62) * mm});
            skLineSegment(sketch, "E149.2.0.2", {"start": v(20.86, -79.52) * mm, "end": v(7.06, -79.52) * mm});
            skLineSegment(sketch, "E149.2.0.3", {"start": v(7.06, -79.52) * mm, "end": v(7.06, -65.72) * mm});
            skLineSegment(sketch, "E149.2.0.4", {"start": v(20.86, -79.52) * mm, "end": v(20.86, -65.72) * mm});
            skLineSegment(sketch, "E149.3.0.0", {"start": v(39.06, -65.72) * mm, "end": v(25.26, -65.72) * mm});
            skPoint(sketch, "E149.3.0.1", {"position": v(32.16, -72.62) * mm});
            skLineSegment(sketch, "E149.3.0.2", {"start": v(39.06, -79.52) * mm, "end": v(25.26, -79.52) * mm});
            skLineSegment(sketch, "E149.3.0.3", {"start": v(25.26, -79.52) * mm, "end": v(25.26, -65.72) * mm});
            skLineSegment(sketch, "E149.3.0.4", {"start": v(39.06, -79.52) * mm, "end": v(39.06, -65.72) * mm});
            skLineSegment(sketch, "E149.4.0.0", {"start": v(57.26, -65.72) * mm, "end": v(43.46, -65.72) * mm});
            skPoint(sketch, "E149.4.0.1", {"position": v(50.36, -72.62) * mm});
            skLineSegment(sketch, "E149.4.0.2", {"start": v(57.26, -79.52) * mm, "end": v(43.46, -79.52) * mm});
            skLineSegment(sketch, "E149.4.0.3", {"start": v(43.46, -79.52) * mm, "end": v(43.46, -65.72) * mm});
            skLineSegment(sketch, "E149.4.0.4", {"start": v(57.26, -79.52) * mm, "end": v(57.26, -65.72) * mm});
            skLineSegment(sketch, "E149.5.0.0", {"start": v(75.46, -65.72) * mm, "end": v(61.66, -65.72) * mm});
            skPoint(sketch, "E149.5.0.1", {"position": v(68.56, -72.62) * mm});
            skLineSegment(sketch, "E149.5.0.2", {"start": v(75.46, -79.52) * mm, "end": v(61.66, -79.52) * mm});
            skLineSegment(sketch, "E149.5.0.3", {"start": v(61.66, -79.52) * mm, "end": v(61.66, -65.72) * mm});
            skLineSegment(sketch, "E149.5.0.4", {"start": v(75.46, -79.52) * mm, "end": v(75.46, -65.72) * mm});
            skLineSegment(sketch, "E149.6.0.0", {"start": v(93.66, -65.72) * mm, "end": v(79.86, -65.72) * mm});
            skPoint(sketch, "E149.6.0.1", {"position": v(86.76, -72.62) * mm});
            skLineSegment(sketch, "E149.6.0.2", {"start": v(93.66, -79.52) * mm, "end": v(79.86, -79.52) * mm});
            skLineSegment(sketch, "E149.6.0.3", {"start": v(79.86, -79.52) * mm, "end": v(79.86, -65.72) * mm});
            skLineSegment(sketch, "E149.6.0.4", {"start": v(93.66, -79.52) * mm, "end": v(93.66, -65.72) * mm});
            skLineSegment(sketch, "E149.7.0.0", {"start": v(111.86, -65.72) * mm, "end": v(98.06, -65.72) * mm});
            skPoint(sketch, "E149.7.0.1", {"position": v(104.96, -72.62) * mm});
            skLineSegment(sketch, "E149.7.0.2", {"start": v(111.86, -79.52) * mm, "end": v(98.06, -79.52) * mm});
            skLineSegment(sketch, "E149.7.0.3", {"start": v(98.06, -79.52) * mm, "end": v(98.06, -65.72) * mm});
            skLineSegment(sketch, "E149.7.0.4", {"start": v(111.86, -79.52) * mm, "end": v(111.86, -65.72) * mm});
            skLineSegment(sketch, "E149.8.0.0", {"start": v(130.06, -65.72) * mm, "end": v(116.26, -65.72) * mm});
            skPoint(sketch, "E149.8.0.1", {"position": v(123.16, -72.62) * mm});
            skLineSegment(sketch, "E149.8.0.2", {"start": v(130.06, -79.52) * mm, "end": v(116.26, -79.52) * mm});
            skLineSegment(sketch, "E149.8.0.3", {"start": v(116.26, -79.52) * mm, "end": v(116.26, -65.72) * mm});
            skLineSegment(sketch, "E149.8.0.4", {"start": v(130.06, -79.52) * mm, "end": v(130.06, -65.72) * mm});
            skLineSegment(sketch, "E149.9.0.0", {"start": v(148.26, -65.72) * mm, "end": v(134.46, -65.72) * mm});
            skPoint(sketch, "E149.9.0.1", {"position": v(141.36, -72.62) * mm});
            skLineSegment(sketch, "E149.9.0.2", {"start": v(148.26, -79.52) * mm, "end": v(134.46, -79.52) * mm});
            skLineSegment(sketch, "E149.9.0.3", {"start": v(134.46, -79.52) * mm, "end": v(134.46, -65.72) * mm});
            skLineSegment(sketch, "E149.9.0.4", {"start": v(148.26, -79.52) * mm, "end": v(148.26, -65.72) * mm});
            skLineSegment(sketch, "E149.direction1", {"start": v(-29.34, -79.52) * mm, "end": v(-11.14, -79.52) * mm, "construction": true});
            skLineSegment(sketch, "E150.bottom", {"start": v(-80.49, -1.45) * mm, "end": v(208.51, -1.45) * mm});
            skLineSegment(sketch, "E150.top", {"start": v(-80.49, -107.7) * mm, "end": v(208.51, -107.7) * mm});
            skLineSegment(sketch, "E150.left", {"start": v(-80.49, -1.45) * mm, "end": v(-80.49, -107.7) * mm});
            skLineSegment(sketch, "E150.right", {"start": v(208.51, -1.45) * mm, "end": v(208.51, -107.7) * mm});
            skSolve(sketch);
        }
        {
            var Q0;
            Q0 = qSketchRegion(id + "F0", true);
            extrude(context, id + "F1", {"entities" : qUnion([Q0]), "oppositeDirection" : true, "depth" : 3 * mm, "offsetDistance" : 25 * mm});
        }
        {
            var Q0;
            Q0=makeQuery(id+"F1.opExtrude","CAP_FACE",FACE,{"disambiguationData":[OSD([sQuery(id+"F0.wireOp",EDGE,"E23.bottom"),sQuery(id+"F0.wireOp",EDGE,"E23.top"),sQuery(id+"F0.wireOp",EDGE,"E23.left"),sQuery(id+"F0.wireOp",EDGE,"E23.right"),sQuery(id+"F0.wireOp",EDGE,"E24.bottom"),sQuery(id+"F0.wireOp",EDGE,"E24.top"),sQuery(id+"F0.wireOp",EDGE,"E24.left"),sQuery(id+"F0.wireOp",EDGE,"E24.right"),sQuery(id+"F0.wireOp",EDGE,"E25.bottom"),sQuery(id+"F0.wireOp",EDGE,"E25.top"),sQuery(id+"F0.wireOp",EDGE,"E25.left"),sQuery(id+"F0.wireOp",EDGE,"E25.right"),sQuery(id+"F0.wireOp",EDGE,"E27.bottom"),sQuery(id+"F0.wireOp",EDGE,"E27.top"),sQuery(id+"F0.wireOp",EDGE,"E27.left"),sQuery(id+"F0.wireOp",EDGE,"E27.right"),sQuery(id+"F0.wireOp",EDGE,"E28.bottom"),sQuery(id+"F0.wireOp",EDGE,"E28.top"),sQuery(id+"F0.wireOp",EDGE,"E28.left"),sQuery(id+"F0.wireOp",EDGE,"E28.right"),sQuery(id+"F0.wireOp",EDGE,"E32"),sQuery(id+"F0.wireOp",EDGE,"E33"),sQuery(id+"F0.wireOp",EDGE,"E34"),sQuery(id+"F0.wireOp",EDGE,"E36"),sQuery(id+"F0.wireOp",EDGE,"E37"),sQuery(id+"F0.wireOp",EDGE,"E38"),sQuery(id+"F0.wireOp",EDGE,"E39"),sQuery(id+"F0.wireOp",EDGE,"E40"),sQuery(id+"F0.wireOp",EDGE,"E41"),sQuery(id+"F0.wireOp",EDGE,"E42"),sQuery(id+"F0.wireOp",EDGE,"E43"),sQuery(id+"F0.wireOp",EDGE,"E44"),sQuery(id+"F0.wireOp",EDGE,"E45"),sQuery(id+"F0.wireOp",EDGE,"E46"),sQuery(id+"F0.wireOp",EDGE,"E47"),sQuery(id+"F0.wireOp",EDGE,"E48"),sQuery(id+"F0.wireOp",EDGE,"E49"),sQuery(id+"F0.wireOp",EDGE,"E50"),sQuery(id+"F0.wireOp",EDGE,"E51"),sQuery(id+"F0.wireOp",EDGE,"E52"),sQuery(id+"F0.wireOp",EDGE,"E53"),sQuery(id+"F0.wireOp",EDGE,"E54"),sQuery(id+"F0.wireOp",EDGE,"E56"),sQuery(id+"F0.wireOp",EDGE,"E57"),sQuery(id+"F0.wireOp",EDGE,"E58"),sQuery(id+"F0.wireOp",EDGE,"E59"),sQuery(id+"F0.wireOp",EDGE,"E60"),sQuery(id+"F0.wireOp",EDGE,"E61"),sQuery(id+"F0.wireOp",EDGE,"E62"),sQuery(id+"F0.wireOp",EDGE,"E63.bottom"),sQuery(id+"F0.wireOp",EDGE,"E63.top"),sQuery(id+"F0.wireOp",EDGE,"E63.left"),sQuery(id+"F0.wireOp",EDGE,"E63.right"),sQuery(id+"F0.wireOp",EDGE,"E64.bottom"),sQuery(id+"F0.wireOp",EDGE,"E64.top"),sQuery(id+"F0.wireOp",EDGE,"E64.left"),sQuery(id+"F0.wireOp",EDGE,"E64.right"),sQuery(id+"F0.wireOp",EDGE,"E65.bottom"),sQuery(id+"F0.wireOp",EDGE,"E65.top"),sQuery(id+"F0.wireOp",EDGE,"E65.left"),sQuery(id+"F0.wireOp",EDGE,"E65.right"),sQuery(id+"F0.wireOp",EDGE,"E66.bottom"),sQuery(id+"F0.wireOp",EDGE,"E66.top"),sQuery(id+"F0.wireOp",EDGE,"E66.left"),sQuery(id+"F0.wireOp",EDGE,"E66.right"),sQuery(id+"F0.wireOp",EDGE,"E67.bottom"),sQuery(id+"F0.wireOp",EDGE,"E67.top"),sQuery(id+"F0.wireOp",EDGE,"E67.left"),sQuery(id+"F0.wireOp",EDGE,"E67.right"),sQuery(id+"F0.wireOp",EDGE,"E68"),sQuery(id+"F0.wireOp",EDGE,"E72"),sQuery(id+"F0.wireOp",EDGE,"E73"),sQuery(id+"F0.wireOp",EDGE,"E74"),sQuery(id+"F0.wireOp",EDGE,"E76"),sQuery(id+"F0.wireOp",EDGE,"E77"),sQuery(id+"F0.wireOp",EDGE,"E78"),sQuery(id+"F0.wireOp",EDGE,"E79"),sQuery(id+"F0.wireOp",EDGE,"E80"),sQuery(id+"F0.wireOp",EDGE,"E81"),sQuery(id+"F0.wireOp",EDGE,"E82"),sQuery(id+"F0.wireOp",EDGE,"E83"),sQuery(id+"F0.wireOp",EDGE,"E84"),sQuery(id+"F0.wireOp",EDGE,"E85"),sQuery(id+"F0.wireOp",EDGE,"E86"),sQuery(id+"F0.wireOp",EDGE,"E87"),sQuery(id+"F0.wireOp",EDGE,"E88"),sQuery(id+"F0.wireOp",EDGE,"E89"),sQuery(id+"F0.wireOp",EDGE,"E90"),sQuery(id+"F0.wireOp",EDGE,"E91"),sQuery(id+"F0.wireOp",EDGE,"E92"),sQuery(id+"F0.wireOp",EDGE,"E93"),sQuery(id+"F0.wireOp",EDGE,"E94"),sQuery(id+"F0.wireOp",EDGE,"E96"),sQuery(id+"F0.wireOp",EDGE,"E97"),sQuery(id+"F0.wireOp",EDGE,"E98"),sQuery(id+"F0.wireOp",EDGE,"E99"),sQuery(id+"F0.wireOp",EDGE,"E100"),sQuery(id+"F0.wireOp",EDGE,"E101"),sQuery(id+"F0.wireOp",EDGE,"E102"),sQuery(id+"F0.wireOp",EDGE,"E103"),sQuery(id+"F0.wireOp",EDGE,"E107"),sQuery(id+"F0.wireOp",EDGE,"E108"),sQuery(id+"F0.wireOp",EDGE,"E109"),sQuery(id+"F0.wireOp",EDGE,"E111"),sQuery(id+"F0.wireOp",EDGE,"E112"),sQuery(id+"F0.wireOp",EDGE,"E113"),sQuery(id+"F0.wireOp",EDGE,"E114"),sQuery(id+"F0.wireOp",EDGE,"E115"),sQuery(id+"F0.wireOp",EDGE,"E116"),sQuery(id+"F0.wireOp",EDGE,"E117"),sQuery(id+"F0.wireOp",EDGE,"E118"),sQuery(id+"F0.wireOp",EDGE,"E119"),sQuery(id+"F0.wireOp",EDGE,"E120"),sQuery(id+"F0.wireOp",EDGE,"E121"),sQuery(id+"F0.wireOp",EDGE,"E122"),sQuery(id+"F0.wireOp",EDGE,"E123"),sQuery(id+"F0.wireOp",EDGE,"E124"),sQuery(id+"F0.wireOp",EDGE,"E125"),sQuery(id+"F0.wireOp",EDGE,"E126"),sQuery(id+"F0.wireOp",EDGE,"E127"),sQuery(id+"F0.wireOp",EDGE,"E128"),sQuery(id+"F0.wireOp",EDGE,"E129"),sQuery(id+"F0.wireOp",EDGE,"E131"),sQuery(id+"F0.wireOp",EDGE,"E132"),sQuery(id+"F0.wireOp",EDGE,"E133"),sQuery(id+"F0.wireOp",EDGE,"E134"),sQuery(id+"F0.wireOp",EDGE,"E135"),sQuery(id+"F0.wireOp",EDGE,"E136"),sQuery(id+"F0.wireOp",EDGE,"E137"),sQuery(id+"F0.wireOp",EDGE,"E138"),sQuery(id+"F0.wireOp",EDGE,"E139.bottom"),sQuery(id+"F0.wireOp",EDGE,"E139.top"),sQuery(id+"F0.wireOp",EDGE,"E139.left"),sQuery(id+"F0.wireOp",EDGE,"E139.right"),sQuery(id+"F0.wireOp",EDGE,"E140.bottom"),sQuery(id+"F0.wireOp",EDGE,"E140.top"),sQuery(id+"F0.wireOp",EDGE,"E140.left"),sQuery(id+"F0.wireOp",EDGE,"E140.right"),sQuery(id+"F0.wireOp",EDGE,"E141.bottom"),sQuery(id+"F0.wireOp",EDGE,"E141.top"),sQuery(id+"F0.wireOp",EDGE,"E141.left"),sQuery(id+"F0.wireOp",EDGE,"E141.right"),sQuery(id+"F0.wireOp",EDGE,"E142.bottom"),sQuery(id+"F0.wireOp",EDGE,"E142.top"),sQuery(id+"F0.wireOp",EDGE,"E142.left"),sQuery(id+"F0.wireOp",EDGE,"E142.right"),sQuery(id+"F0.wireOp",EDGE,"E143.1.0.0"),sQuery(id+"F0.wireOp",EDGE,"E143.1.0.1"),sQuery(id+"F0.wireOp",EDGE,"E143.1.0.2"),sQuery(id+"F0.wireOp",EDGE,"E143.1.0.3"),sQuery(id+"F0.wireOp",EDGE,"E143.2.0.0"),sQuery(id+"F0.wireOp",EDGE,"E143.2.0.1"),sQuery(id+"F0.wireOp",EDGE,"E143.2.0.2"),sQuery(id+"F0.wireOp",EDGE,"E143.2.0.3"),sQuery(id+"F0.wireOp",EDGE,"E143.3.0.0"),sQuery(id+"F0.wireOp",EDGE,"E143.3.0.1"),sQuery(id+"F0.wireOp",EDGE,"E143.3.0.2"),sQuery(id+"F0.wireOp",EDGE,"E143.3.0.3"),sQuery(id+"F0.wireOp",EDGE,"E143.4.0.0"),sQuery(id+"F0.wireOp",EDGE,"E143.4.0.1"),sQuery(id+"F0.wireOp",EDGE,"E143.4.0.2"),sQuery(id+"F0.wireOp",EDGE,"E143.4.0.3"),sQuery(id+"F0.wireOp",EDGE,"E143.5.0.0"),sQuery(id+"F0.wireOp",EDGE,"E143.5.0.1"),sQuery(id+"F0.wireOp",EDGE,"E143.5.0.2"),sQuery(id+"F0.wireOp",EDGE,"E143.5.0.3"),sQuery(id+"F0.wireOp",EDGE,"E143.6.0.0"),sQuery(id+"F0.wireOp",EDGE,"E143.6.0.1"),sQuery(id+"F0.wireOp",EDGE,"E143.6.0.2"),sQuery(id+"F0.wireOp",EDGE,"E143.6.0.3"),sQuery(id+"F0.wireOp",EDGE,"E143.7.0.0"),sQuery(id+"F0.wireOp",EDGE,"E143.7.0.1"),sQuery(id+"F0.wireOp",EDGE,"E143.7.0.2"),sQuery(id+"F0.wireOp",EDGE,"E143.7.0.3"),sQuery(id+"F0.wireOp",EDGE,"E143.8.0.0"),sQuery(id+"F0.wireOp",EDGE,"E143.8.0.1"),sQuery(id+"F0.wireOp",EDGE,"E143.8.0.2"),sQuery(id+"F0.wireOp",EDGE,"E143.8.0.3"),sQuery(id+"F0.wireOp",EDGE,"E143.9.0.0"),sQuery(id+"F0.wireOp",EDGE,"E143.9.0.1"),sQuery(id+"F0.wireOp",EDGE,"E143.9.0.2"),sQuery(id+"F0.wireOp",EDGE,"E143.9.0.3"),sQuery(id+"F0.wireOp",EDGE,"E143.10.0.0"),sQuery(id+"F0.wireOp",EDGE,"E143.10.0.1"),sQuery(id+"F0.wireOp",EDGE,"E143.10.0.2"),sQuery(id+"F0.wireOp",EDGE,"E143.10.0.3"),sQuery(id+"F0.wireOp",EDGE,"E143.11.0.0"),sQuery(id+"F0.wireOp",EDGE,"E143.11.0.1"),sQuery(id+"F0.wireOp",EDGE,"E143.11.0.2"),sQuery(id+"F0.wireOp",EDGE,"E143.11.0.3"),sQuery(id+"F0.wireOp",EDGE,"E143.12.0.0"),sQuery(id+"F0.wireOp",EDGE,"E143.12.0.1"),sQuery(id+"F0.wireOp",EDGE,"E143.12.0.2"),sQuery(id+"F0.wireOp",EDGE,"E143.12.0.3"),sQuery(id+"F0.wireOp",EDGE,"E143.13.0.0"),sQuery(id+"F0.wireOp",EDGE,"E143.13.0.1"),sQuery(id+"F0.wireOp",EDGE,"E143.13.0.2"),sQuery(id+"F0.wireOp",EDGE,"E143.13.0.3"),sQuery(id+"F0.wireOp",EDGE,"E143.14.0.0"),sQuery(id+"F0.wireOp",EDGE,"E143.14.0.1"),sQuery(id+"F0.wireOp",EDGE,"E143.14.0.2"),sQuery(id+"F0.wireOp",EDGE,"E143.14.0.3"),sQuery(id+"F0.wireOp",EDGE,"E144.bottom"),sQuery(id+"F0.wireOp",EDGE,"E144.top"),sQuery(id+"F0.wireOp",EDGE,"E144.left"),sQuery(id+"F0.wireOp",EDGE,"E144.right"),sQuery(id+"F0.wireOp",EDGE,"E145.bottom"),sQuery(id+"F0.wireOp",EDGE,"E145.top"),sQuery(id+"F0.wireOp",EDGE,"E145.left"),sQuery(id+"F0.wireOp",EDGE,"E145.right"),sQuery(id+"F0.wireOp",EDGE,"E146.bottom"),sQuery(id+"F0.wireOp",EDGE,"E146.top"),sQuery(id+"F0.wireOp",EDGE,"E146.left"),sQuery(id+"F0.wireOp",EDGE,"E146.right"),sQuery(id+"F0.wireOp",EDGE,"E147.1.0.0"),sQuery(id+"F0.wireOp",EDGE,"E147.1.0.1"),sQuery(id+"F0.wireOp",EDGE,"E147.1.0.2"),sQuery(id+"F0.wireOp",EDGE,"E147.1.0.3"),sQuery(id+"F0.wireOp",EDGE,"E147.2.0.0"),sQuery(id+"F0.wireOp",EDGE,"E147.2.0.1"),sQuery(id+"F0.wireOp",EDGE,"E147.2.0.2"),sQuery(id+"F0.wireOp",EDGE,"E147.2.0.3"),sQuery(id+"F0.wireOp",EDGE,"E147.3.0.0"),sQuery(id+"F0.wireOp",EDGE,"E147.3.0.1"),sQuery(id+"F0.wireOp",EDGE,"E147.3.0.2"),sQuery(id+"F0.wireOp",EDGE,"E147.3.0.3"),sQuery(id+"F0.wireOp",EDGE,"E147.4.0.0"),sQuery(id+"F0.wireOp",EDGE,"E147.4.0.1"),sQuery(id+"F0.wireOp",EDGE,"E147.4.0.2"),sQuery(id+"F0.wireOp",EDGE,"E147.4.0.3"),sQuery(id+"F0.wireOp",EDGE,"E147.5.0.0"),sQuery(id+"F0.wireOp",EDGE,"E147.5.0.1"),sQuery(id+"F0.wireOp",EDGE,"E147.5.0.2"),sQuery(id+"F0.wireOp",EDGE,"E147.5.0.3"),sQuery(id+"F0.wireOp",EDGE,"E147.6.0.0"),sQuery(id+"F0.wireOp",EDGE,"E147.6.0.1"),sQuery(id+"F0.wireOp",EDGE,"E147.6.0.2"),sQuery(id+"F0.wireOp",EDGE,"E147.6.0.3"),sQuery(id+"F0.wireOp",EDGE,"E147.7.0.0"),sQuery(id+"F0.wireOp",EDGE,"E147.7.0.1"),sQuery(id+"F0.wireOp",EDGE,"E147.7.0.2"),sQuery(id+"F0.wireOp",EDGE,"E147.7.0.3"),sQuery(id+"F0.wireOp",EDGE,"E147.8.0.0"),sQuery(id+"F0.wireOp",EDGE,"E147.8.0.1"),sQuery(id+"F0.wireOp",EDGE,"E147.8.0.2"),sQuery(id+"F0.wireOp",EDGE,"E147.8.0.3"),sQuery(id+"F0.wireOp",EDGE,"E147.9.0.0"),sQuery(id+"F0.wireOp",EDGE,"E147.9.0.1"),sQuery(id+"F0.wireOp",EDGE,"E147.9.0.2"),sQuery(id+"F0.wireOp",EDGE,"E147.9.0.3"),sQuery(id+"F0.wireOp",EDGE,"E147.10.0.0"),sQuery(id+"F0.wireOp",EDGE,"E147.10.0.1"),sQuery(id+"F0.wireOp",EDGE,"E147.10.0.2"),sQuery(id+"F0.wireOp",EDGE,"E147.10.0.3"),sQuery(id+"F0.wireOp",EDGE,"E147.11.0.0"),sQuery(id+"F0.wireOp",EDGE,"E147.11.0.1"),sQuery(id+"F0.wireOp",EDGE,"E147.11.0.2"),sQuery(id+"F0.wireOp",EDGE,"E147.11.0.3"),sQuery(id+"F0.wireOp",EDGE,"E148.1.0.1"),sQuery(id+"F0.wireOp",EDGE,"E148.1.0.2"),sQuery(id+"F0.wireOp",EDGE,"E148.1.0.3"),sQuery(id+"F0.wireOp",EDGE,"E148.1.0.4"),sQuery(id+"F0.wireOp",EDGE,"E148.2.0.1"),sQuery(id+"F0.wireOp",EDGE,"E148.2.0.2"),sQuery(id+"F0.wireOp",EDGE,"E148.2.0.3"),sQuery(id+"F0.wireOp",EDGE,"E148.2.0.4"),sQuery(id+"F0.wireOp",EDGE,"E148.3.0.1"),sQuery(id+"F0.wireOp",EDGE,"E148.3.0.2"),sQuery(id+"F0.wireOp",EDGE,"E148.3.0.3"),sQuery(id+"F0.wireOp",EDGE,"E148.3.0.4"),sQuery(id+"F0.wireOp",EDGE,"E148.4.0.1"),sQuery(id+"F0.wireOp",EDGE,"E148.4.0.2"),sQuery(id+"F0.wireOp",EDGE,"E148.4.0.3"),sQuery(id+"F0.wireOp",EDGE,"E148.4.0.4"),sQuery(id+"F0.wireOp",EDGE,"E148.5.0.1"),sQuery(id+"F0.wireOp",EDGE,"E148.5.0.2"),sQuery(id+"F0.wireOp",EDGE,"E148.5.0.3"),sQuery(id+"F0.wireOp",EDGE,"E148.5.0.4"),sQuery(id+"F0.wireOp",EDGE,"E148.6.0.1"),sQuery(id+"F0.wireOp",EDGE,"E148.6.0.2"),sQuery(id+"F0.wireOp",EDGE,"E148.6.0.3"),sQuery(id+"F0.wireOp",EDGE,"E148.6.0.4"),sQuery(id+"F0.wireOp",EDGE,"E148.7.0.1"),sQuery(id+"F0.wireOp",EDGE,"E148.7.0.2"),sQuery(id+"F0.wireOp",EDGE,"E148.7.0.3"),sQuery(id+"F0.wireOp",EDGE,"E148.7.0.4"),sQuery(id+"F0.wireOp",EDGE,"E148.8.0.1"),sQuery(id+"F0.wireOp",EDGE,"E148.8.0.2"),sQuery(id+"F0.wireOp",EDGE,"E148.8.0.3"),sQuery(id+"F0.wireOp",EDGE,"E148.8.0.4"),sQuery(id+"F0.wireOp",EDGE,"E148.9.0.1"),sQuery(id+"F0.wireOp",EDGE,"E148.9.0.2"),sQuery(id+"F0.wireOp",EDGE,"E148.9.0.3"),sQuery(id+"F0.wireOp",EDGE,"E148.9.0.4"),sQuery(id+"F0.wireOp",EDGE,"E148.10.0.1"),sQuery(id+"F0.wireOp",EDGE,"E148.10.0.2"),sQuery(id+"F0.wireOp",EDGE,"E148.10.0.3"),sQuery(id+"F0.wireOp",EDGE,"E148.10.0.4"),sQuery(id+"F0.wireOp",EDGE,"E149.1.0.0"),sQuery(id+"F0.wireOp",EDGE,"E149.1.0.2"),sQuery(id+"F0.wireOp",EDGE,"E149.1.0.3"),sQuery(id+"F0.wireOp",EDGE,"E149.1.0.4"),sQuery(id+"F0.wireOp",EDGE,"E149.2.0.0"),sQuery(id+"F0.wireOp",EDGE,"E149.2.0.2"),sQuery(id+"F0.wireOp",EDGE,"E149.2.0.3"),sQuery(id+"F0.wireOp",EDGE,"E149.2.0.4"),sQuery(id+"F0.wireOp",EDGE,"E149.3.0.0"),sQuery(id+"F0.wireOp",EDGE,"E149.3.0.2"),sQuery(id+"F0.wireOp",EDGE,"E149.3.0.3"),sQuery(id+"F0.wireOp",EDGE,"E149.3.0.4"),sQuery(id+"F0.wireOp",EDGE,"E149.4.0.0"),sQuery(id+"F0.wireOp",EDGE,"E149.4.0.2"),sQuery(id+"F0.wireOp",EDGE,"E149.4.0.3"),sQuery(id+"F0.wireOp",EDGE,"E149.4.0.4"),sQuery(id+"F0.wireOp",EDGE,"E149.5.0.0"),sQuery(id+"F0.wireOp",EDGE,"E149.5.0.2"),sQuery(id+"F0.wireOp",EDGE,"E149.5.0.3"),sQuery(id+"F0.wireOp",EDGE,"E149.5.0.4"),sQuery(id+"F0.wireOp",EDGE,"E149.6.0.0"),sQuery(id+"F0.wireOp",EDGE,"E149.6.0.2"),sQuery(id+"F0.wireOp",EDGE,"E149.6.0.3"),sQuery(id+"F0.wireOp",EDGE,"E149.6.0.4"),sQuery(id+"F0.wireOp",EDGE,"E149.7.0.0"),sQuery(id+"F0.wireOp",EDGE,"E149.7.0.2"),sQuery(id+"F0.wireOp",EDGE,"E149.7.0.3"),sQuery(id+"F0.wireOp",EDGE,"E149.7.0.4"),sQuery(id+"F0.wireOp",EDGE,"E149.8.0.0"),sQuery(id+"F0.wireOp",EDGE,"E149.8.0.2"),sQuery(id+"F0.wireOp",EDGE,"E149.8.0.3"),sQuery(id+"F0.wireOp",EDGE,"E149.8.0.4"),sQuery(id+"F0.wireOp",EDGE,"E149.9.0.0"),sQuery(id+"F0.wireOp",EDGE,"E149.9.0.2"),sQuery(id+"F0.wireOp",EDGE,"E149.9.0.3"),sQuery(id+"F0.wireOp",EDGE,"E149.9.0.4"),sQuery(id+"F0.wireOp",EDGE,"E150.bottom"),sQuery(id+"F0.wireOp",EDGE,"E150.top"),sQuery(id+"F0.wireOp",EDGE,"E150.left"),sQuery(id+"F0.wireOp",EDGE,"E150.right")])],"isStart":false});
            var sketch = newSketch(context, id + "F2", { "sketchPlane" : qUnion([Q0])});
            skLineSegment(sketch, "E151.bottom", {"start": v(-23.04, 99.17) * mm, "end": v(-40.04, 99.17) * mm, "construction": true});
            skLineSegment(sketch, "E151.top", {"start": v(-23.04, 82.17) * mm, "end": v(-40.04, 82.17) * mm, "construction": true});
            skLineSegment(sketch, "E151.left", {"start": v(-23.04, 99.17) * mm, "end": v(-23.04, 82.17) * mm, "construction": true});
            skLineSegment(sketch, "E151.right", {"start": v(-40.04, 99.17) * mm, "end": v(-40.04, 82.17) * mm, "construction": true});
            skPoint(sketch, "E151.middle", {"position": v(-31.54, 90.67) * mm});
            skPoint(sketch, "E151.middle.positionSnap0", {"position": v(-24.64, 90.67) * mm});
            skPoint(sketch, "E151.middle.positionSnap1", {"position": v(-31.54, 97.57) * mm});
            skPoint(sketch, "E151.centerSnap0", {"position": v(-24.64, 90.67) * mm});
            skPoint(sketch, "E151.centerSnap1", {"position": v(-31.54, 97.57) * mm});
            skLineSegment(sketch, "E152.bottom", {"start": v(-34.01, 64.12) * mm, "end": v(-70.01, 64.12) * mm, "construction": true});
            skLineSegment(sketch, "E152.top", {"start": v(-34.01, 81.12) * mm, "end": v(-70.01, 81.12) * mm, "construction": true});
            skLineSegment(sketch, "E152.left", {"start": v(-34.01, 64.12) * mm, "end": v(-34.01, 81.12) * mm, "construction": true});
            skLineSegment(sketch, "E152.right", {"start": v(-70.01, 64.12) * mm, "end": v(-70.01, 81.12) * mm, "construction": true});
            skPoint(sketch, "E152.middle", {"position": v(-52.01, 72.62) * mm});
            skPoint(sketch, "E152.middle.positionSnap0", {"position": v(-29.34, 72.62) * mm});
            skPoint(sketch, "E152.middle.positionSnap1", {"position": v(-52.01, 65.72) * mm});
            skPoint(sketch, "E152.centerSnap0", {"position": v(-29.34, 72.62) * mm});
            skPoint(sketch, "E152.centerSnap1", {"position": v(-52.01, 65.72) * mm});
            skLineSegment(sketch, "E153.bottom", {"start": v(-54.89, 9.97) * mm, "end": v(-71.89, 9.97) * mm, "construction": true});
            skLineSegment(sketch, "E153.top", {"start": v(-54.89, 26.97) * mm, "end": v(-71.89, 26.97) * mm, "construction": true});
            skLineSegment(sketch, "E153.left", {"start": v(-54.89, 9.97) * mm, "end": v(-54.89, 26.97) * mm, "construction": true});
            skLineSegment(sketch, "E153.right", {"start": v(-71.89, 9.97) * mm, "end": v(-71.89, 26.97) * mm, "construction": true});
            skPoint(sketch, "E153.middle", {"position": v(-63.39, 18.47) * mm});
            skPoint(sketch, "E153.middle.positionSnap0", {"position": v(-56.49, 18.47) * mm});
            skPoint(sketch, "E153.middle.positionSnap1", {"position": v(-63.39, 11.57) * mm});
            skPoint(sketch, "E153.centerSnap0", {"position": v(-56.49, 18.47) * mm});
            skPoint(sketch, "E153.centerSnap1", {"position": v(-63.39, 11.57) * mm});
            skLineSegment(sketch, "E154.bottom", {"start": v(199.91, 9.97) * mm, "end": v(182.91, 9.97) * mm, "construction": true});
            skLineSegment(sketch, "E154.top", {"start": v(199.91, 26.97) * mm, "end": v(182.91, 26.97) * mm, "construction": true});
            skLineSegment(sketch, "E154.left", {"start": v(199.91, 9.97) * mm, "end": v(199.91, 26.97) * mm, "construction": true});
            skLineSegment(sketch, "E154.right", {"start": v(182.91, 9.97) * mm, "end": v(182.91, 26.97) * mm, "construction": true});
            skPoint(sketch, "E154.middle", {"position": v(191.41, 18.47) * mm});
            skPoint(sketch, "E154.middle.positionSnap0", {"position": v(198.31, 18.47) * mm});
            skPoint(sketch, "E154.middle.positionSnap1", {"position": v(191.41, 25.37) * mm});
            skPoint(sketch, "E154.centerSnap0", {"position": v(198.31, 18.47) * mm});
            skPoint(sketch, "E154.centerSnap1", {"position": v(191.41, 25.37) * mm});
            skLineSegment(sketch, "E155.bottom", {"start": v(149.86, 82.17) * mm, "end": v(132.86, 82.17) * mm, "construction": true});
            skLineSegment(sketch, "E155.top", {"start": v(149.86, 99.17) * mm, "end": v(132.86, 99.17) * mm, "construction": true});
            skLineSegment(sketch, "E155.left", {"start": v(149.86, 82.17) * mm, "end": v(149.86, 99.17) * mm, "construction": true});
            skLineSegment(sketch, "E155.right", {"start": v(132.86, 82.17) * mm, "end": v(132.86, 99.17) * mm, "construction": true});
            skPoint(sketch, "E155.middle", {"position": v(141.36, 90.67) * mm});
            skPoint(sketch, "E155.middle.positionSnap0", {"position": v(141.36, 97.57) * mm});
            skPoint(sketch, "E155.middle.positionSnap1", {"position": v(148.26, 90.67) * mm});
            skPoint(sketch, "E155.centerSnap0", {"position": v(141.36, 97.57) * mm});
            skPoint(sketch, "E155.centerSnap1", {"position": v(148.26, 90.67) * mm});
            skLineSegment(sketch, "E156.bottom", {"start": v(199.91, 64.12) * mm, "end": v(182.91, 64.12) * mm, "construction": true});
            skLineSegment(sketch, "E156.top", {"start": v(199.91, 81.12) * mm, "end": v(182.91, 81.12) * mm, "construction": true});
            skLineSegment(sketch, "E156.left", {"start": v(199.91, 64.12) * mm, "end": v(199.91, 81.12) * mm, "construction": true});
            skLineSegment(sketch, "E156.right", {"start": v(182.91, 64.12) * mm, "end": v(182.91, 81.12) * mm, "construction": true});
            skPoint(sketch, "E156.middle", {"position": v(191.41, 72.62) * mm});
            skPoint(sketch, "E156.middle.positionSnap0", {"position": v(198.31, 72.62) * mm});
            skPoint(sketch, "E156.middle.positionSnap1", {"position": v(191.41, 79.52) * mm});
            skPoint(sketch, "E156.centerSnap0", {"position": v(198.31, 72.62) * mm});
            skPoint(sketch, "E156.centerSnap1", {"position": v(191.41, 79.52) * mm});
            skLineSegment(sketch, "E157", {"start": v(-40.04, 99.17) * mm, "end": v(-40.04, 82.17) * mm});
            skLineSegment(sketch, "E158", {"start": v(-40.04, 82.17) * mm, "end": v(-71.89, 82.17) * mm});
            skLineSegment(sketch, "E159", {"start": v(-71.89, 82.17) * mm, "end": v(-71.89, 9.97) * mm});
            skLineSegment(sketch, "E160", {"start": v(-71.89, 9.97) * mm, "end": v(199.91, 9.97) * mm});
            skLineSegment(sketch, "E161", {"start": v(199.91, 9.97) * mm, "end": v(199.91, 82.17) * mm});
            skLineSegment(sketch, "E162", {"start": v(199.91, 82.17) * mm, "end": v(149.86, 82.17) * mm});
            skLineSegment(sketch, "E163", {"start": v(149.86, 82.17) * mm, "end": v(149.86, 99.17) * mm});
            skLineSegment(sketch, "E164", {"start": v(149.86, 99.17) * mm, "end": v(-40.04, 99.17) * mm});
            skSolve(sketch);
        }
        {
            var Q0;
            Q0 = qSketchRegion(id + "F2", true);
            extrude(context, id + "F3", {"entities" : qUnion([Q0]), "operationType" : NewBodyOperationType.REMOVE, "oppositeDirection" : true, "depth" : 1.65 * mm, "offsetDistance" : 25 * mm});
        }
        {
            var Q0;
            Q0=makeQuery(id+"F1.opExtrude","SWEPT_EDGE",EDGE,{"disambiguationData":[OSD([sQuery(id+"F0.wireOp",EDGE,"E150.top"),sQuery(id+"F0.wireOp",EDGE,"E150.left")])]});
            var Q1;
            Q1=makeQuery(id+"F1.opExtrude","SWEPT_EDGE",EDGE,{"disambiguationData":[OSD([sQuery(id+"F0.wireOp",EDGE,"E150.bottom"),sQuery(id+"F0.wireOp",EDGE,"E150.left")])]});
            var Q2;
            Q2=makeQuery(id+"F1.opExtrude","SWEPT_EDGE",EDGE,{"disambiguationData":[OSD([sQuery(id+"F0.wireOp",EDGE,"E150.top"),sQuery(id+"F0.wireOp",EDGE,"E150.right")])]});
            var Q3;
            Q3=makeQuery(id+"F1.opExtrude","SWEPT_EDGE",EDGE,{"disambiguationData":[OSD([sQuery(id+"F0.wireOp",EDGE,"E150.bottom"),sQuery(id+"F0.wireOp",EDGE,"E150.right")])]});
            fillet(context, id + "F4", {"entities" : qUnion([Q0, Q1, Q2, Q3]), "radius" : 4 * mm, "tangentPropagation" : true, "allowEdgeOverflow" : false});
        }
    });
